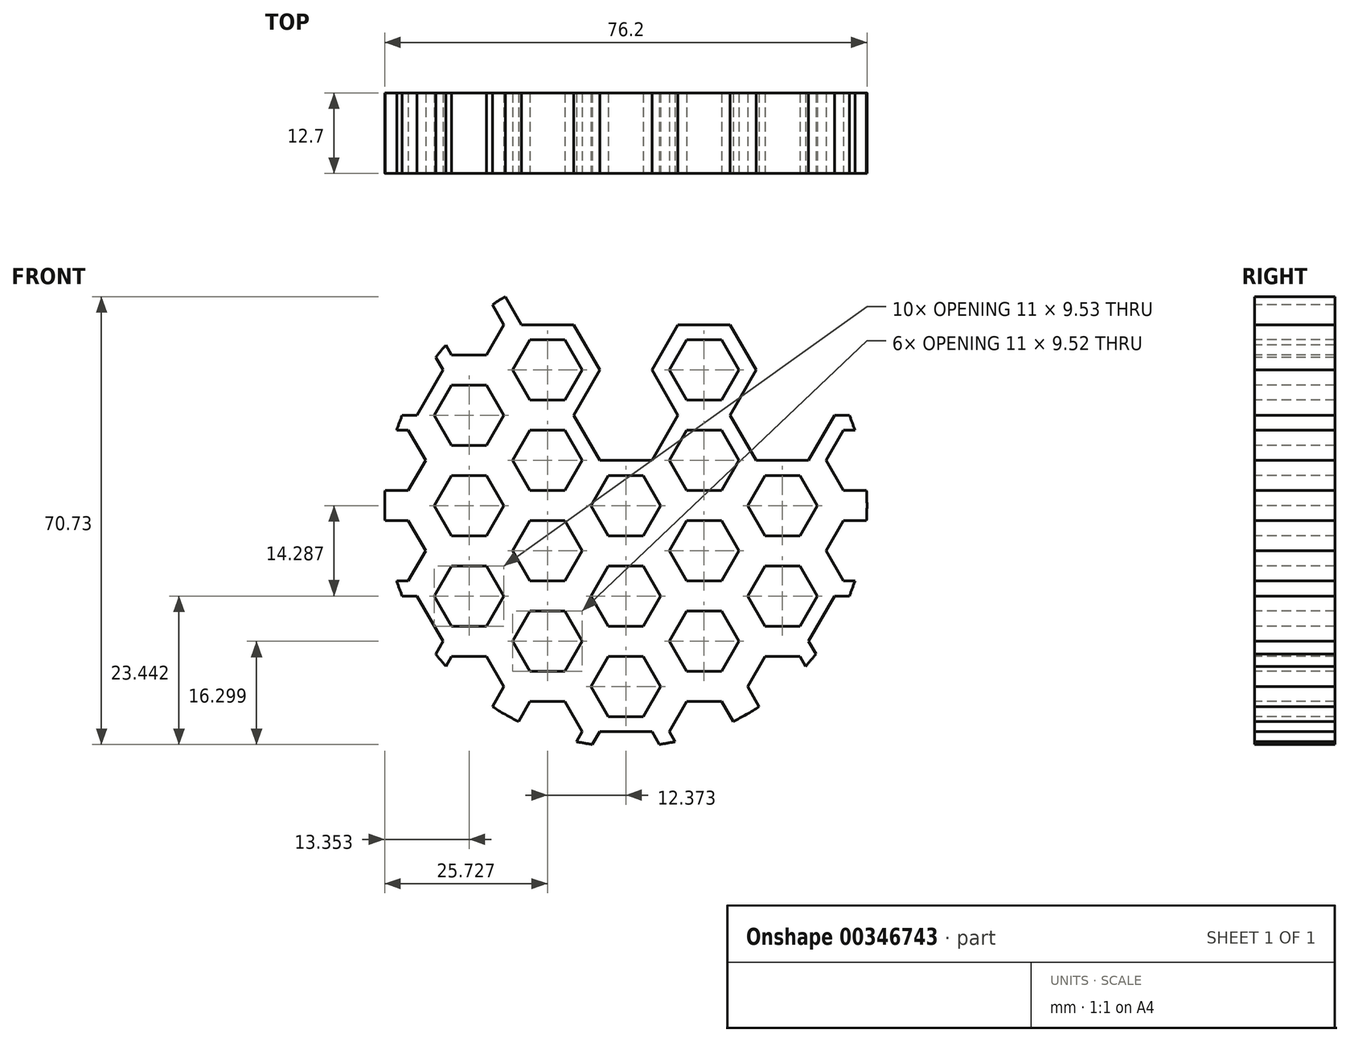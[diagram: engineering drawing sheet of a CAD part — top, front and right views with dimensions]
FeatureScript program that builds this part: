
annotation { "Feature Type Name" : "Feature", "Feature Type Description" : "" }
export const myFeature = defineFeature(function(context is Context, id is Id, definition is map)
    precondition{}
    {
        {
            var Q0;
            Q0=qCreatedBy(makeId("Front.planeOp"),FACE);
            var sketch = newSketch(context, id + "F0", { "sketchPlane" : qUnion([Q0])});
            skCircle(sketch, "E0.cCircle", {"center": v(0, 0) * mm, "radius": 4.76 * mm, "construction": true});
            skLineSegment(sketch, "E0.0", {"start": v(2.75, -4.76) * mm, "end": v(-2.75, -4.76) * mm});
            skLineSegment(sketch, "E0.1", {"start": v(-2.75, -4.76) * mm, "end": v(-5.5, 0) * mm});
            skLineSegment(sketch, "E0.2", {"start": v(-5.5, 0) * mm, "end": v(-2.75, 4.76) * mm});
            skLineSegment(sketch, "E0.3", {"start": v(-2.75, 4.76) * mm, "end": v(2.75, 4.76) * mm});
            skLineSegment(sketch, "E0.4", {"start": v(2.75, 4.76) * mm, "end": v(5.5, 0) * mm});
            skLineSegment(sketch, "E0.5", {"start": v(5.5, 0) * mm, "end": v(2.75, -4.76) * mm});
            skPoint(sketch, "E0.0.midPoint", {"position": v(0, -4.76) * mm});
            skCircle(sketch, "E1.cCircle", {"center": v(0, 0) * mm, "radius": 7.14 * mm, "construction": true});
            skLineSegment(sketch, "E1.0", {"start": v(4.12, -7.14) * mm, "end": v(-4.12, -7.14) * mm});
            skLineSegment(sketch, "E1.1", {"start": v(-4.12, -7.14) * mm, "end": v(-8.25, 0) * mm});
            skLineSegment(sketch, "E1.2", {"start": v(-8.25, 0) * mm, "end": v(-4.12, 7.14) * mm});
            skLineSegment(sketch, "E1.3", {"start": v(-4.12, 7.14) * mm, "end": v(4.12, 7.14) * mm});
            skLineSegment(sketch, "E1.4", {"start": v(4.12, 7.14) * mm, "end": v(8.25, 0) * mm});
            skLineSegment(sketch, "E1.5", {"start": v(8.25, 0) * mm, "end": v(4.12, -7.14) * mm});
            skPoint(sketch, "E1.0.midPoint", {"position": v(0, -7.14) * mm});
            skLineSegment(sketch, "E2.MirrorCS", {"start": v(17.87, 7.14) * mm, "end": v(15.12, 11.9) * mm});
            skLineSegment(sketch, "E3.MirrorCS", {"start": v(8.25, 0) * mm, "end": v(16.5, 0) * mm});
            skLineSegment(sketch, "E4.MirrorCS", {"start": v(15.12, 2.38) * mm, "end": v(17.87, 7.14) * mm});
            skPoint(sketch, "E5.MirrorP", {"position": v(16.5, 4.76) * mm});
            skLineSegment(sketch, "E6.MirrorCS", {"start": v(20.62, 7.14) * mm, "end": v(16.5, 14.29) * mm});
            skLineSegment(sketch, "E7.MirrorCS", {"start": v(16.5, 0) * mm, "end": v(20.62, 7.14) * mm});
            skLineSegment(sketch, "E8.MirrorCS", {"start": v(8.25, 14.29) * mm, "end": v(4.12, 7.14) * mm});
            skLineSegment(sketch, "E9.MirrorCS", {"start": v(16.5, 14.29) * mm, "end": v(8.25, 14.29) * mm});
            skLineSegment(sketch, "E10.MirrorCS", {"start": v(9.62, 11.9) * mm, "end": v(6.87, 7.14) * mm});
            skPoint(sketch, "E11.MirrorP", {"position": v(18.56, 3.57) * mm});
            skLineSegment(sketch, "E12.MirrorCS", {"start": v(6.87, 7.14) * mm, "end": v(9.62, 2.38) * mm});
            skLineSegment(sketch, "E13.MirrorCS", {"start": v(9.62, 2.38) * mm, "end": v(15.12, 2.38) * mm});
            skCircle(sketch, "E14.MirrorC", {"center": v(12.37, 7.14) * mm, "radius": 4.76 * mm, "construction": true});
            skCircle(sketch, "E15.MirrorC", {"center": v(12.37, 7.14) * mm, "radius": 7.14 * mm, "construction": true});
            skLineSegment(sketch, "E16.MirrorCS", {"start": v(15.12, 11.9) * mm, "end": v(9.62, 11.9) * mm});
            skLineSegment(sketch, "E17.MirrorCS", {"start": v(15.12, -2.38) * mm, "end": v(17.87, -7.14) * mm});
            skLineSegment(sketch, "E18.MirrorCS", {"start": v(20.62, -7.14) * mm, "end": v(16.5, -14.29) * mm});
            skPoint(sketch, "E19.MirrorP", {"position": v(16.5, -4.76) * mm});
            skLineSegment(sketch, "E20.MirrorCS", {"start": v(8.25, -14.29) * mm, "end": v(4.12, -7.14) * mm});
            skCircle(sketch, "E21.MirrorC", {"center": v(12.37, -7.14) * mm, "radius": 7.14 * mm, "construction": true});
            skLineSegment(sketch, "E22.MirrorCS", {"start": v(17.87, -7.14) * mm, "end": v(15.12, -11.9) * mm});
            skLineSegment(sketch, "E23.MirrorCS", {"start": v(4.12, -7.14) * mm, "end": v(8.25, 0) * mm});
            skLineSegment(sketch, "E24.MirrorCS", {"start": v(16.5, -14.29) * mm, "end": v(8.25, -14.29) * mm});
            skLineSegment(sketch, "E25.MirrorCS", {"start": v(6.87, -7.14) * mm, "end": v(9.62, -2.38) * mm});
            skLineSegment(sketch, "E26.MirrorCS", {"start": v(9.62, -11.9) * mm, "end": v(6.87, -7.14) * mm});
            skLineSegment(sketch, "E27.MirrorCS", {"start": v(16.5, 0) * mm, "end": v(20.62, -7.14) * mm});
            skCircle(sketch, "E28.MirrorC", {"center": v(12.37, -7.14) * mm, "radius": 4.76 * mm, "construction": true});
            skLineSegment(sketch, "E29.MirrorCS", {"start": v(15.12, -11.9) * mm, "end": v(9.62, -11.9) * mm});
            skLineSegment(sketch, "E30.MirrorCS", {"start": v(2.75, -4.76) * mm, "end": v(5.5, 0) * mm});
            skLineSegment(sketch, "E31.MirrorCS", {"start": v(9.62, -2.38) * mm, "end": v(15.12, -2.38) * mm});
            skPoint(sketch, "E32.MirrorP", {"position": v(18.56, -3.57) * mm});
            skCircle(sketch, "E33", {"center": v(0, 0) * mm, "radius": 38.1 * mm});
            skLineSegment(sketch, "E34.MirrorCS", {"start": v(15.12, 26.2) * mm, "end": v(17.87, 21.43) * mm});
            skLineSegment(sketch, "E35.MirrorCS", {"start": v(16.5, 28.58) * mm, "end": v(20.62, 21.43) * mm});
            skCircle(sketch, "E36.MirrorC", {"center": v(12.37, 21.43) * mm, "radius": 7.14 * mm, "construction": true});
            skLineSegment(sketch, "E37.MirrorCS", {"start": v(9.62, 16.67) * mm, "end": v(6.87, 21.43) * mm});
            skLineSegment(sketch, "E38.MirrorCS", {"start": v(9.62, 26.2) * mm, "end": v(15.12, 26.2) * mm});
            skLineSegment(sketch, "E39.MirrorCS", {"start": v(6.87, 21.43) * mm, "end": v(9.62, 26.2) * mm});
            skLineSegment(sketch, "E40.MirrorCS", {"start": v(4.12, 21.43) * mm, "end": v(8.25, 28.58) * mm});
            skCircle(sketch, "E41.MirrorC", {"center": v(12.37, 21.43) * mm, "radius": 4.76 * mm, "construction": true});
            skLineSegment(sketch, "E42.MirrorCS", {"start": v(20.62, 21.43) * mm, "end": v(16.5, 14.29) * mm});
            skPoint(sketch, "E43.MirrorP", {"position": v(16.5, 23.81) * mm});
            skPoint(sketch, "E44.MirrorP", {"position": v(18.56, 25) * mm});
            skLineSegment(sketch, "E45.MirrorCS", {"start": v(8.25, 14.29) * mm, "end": v(4.12, 21.43) * mm});
            skLineSegment(sketch, "E46.MirrorCS", {"start": v(15.12, 16.67) * mm, "end": v(9.62, 16.67) * mm});
            skLineSegment(sketch, "E47.MirrorCS", {"start": v(8.25, 28.58) * mm, "end": v(16.5, 28.58) * mm});
            skLineSegment(sketch, "E48.MirrorCS", {"start": v(17.87, 21.43) * mm, "end": v(15.12, 16.67) * mm});
            skLineSegment(sketch, "E49.MirrorCS", {"start": v(4.12, 7.14) * mm, "end": v(-4.12, 7.14) * mm});
            skLineSegment(sketch, "E50.MirrorCS", {"start": v(2.75, 19.05) * mm, "end": v(5.5, 14.29) * mm});
            skLineSegment(sketch, "E51.MirrorCS", {"start": v(4.12, 21.43) * mm, "end": v(8.25, 14.29) * mm});
            skCircle(sketch, "E52.MirrorC", {"center": v(0, 14.29) * mm, "radius": 7.14 * mm, "construction": true});
            skLineSegment(sketch, "E53.MirrorCS", {"start": v(-2.75, 9.52) * mm, "end": v(-5.5, 14.29) * mm});
            skLineSegment(sketch, "E54.MirrorCS", {"start": v(-2.75, 19.05) * mm, "end": v(2.75, 19.05) * mm});
            skLineSegment(sketch, "E55.MirrorCS", {"start": v(-5.5, 14.29) * mm, "end": v(-2.75, 19.05) * mm});
            skLineSegment(sketch, "E56.MirrorCS", {"start": v(-8.25, 14.29) * mm, "end": v(-4.12, 21.43) * mm});
            skCircle(sketch, "E57.MirrorC", {"center": v(0, 14.29) * mm, "radius": 4.76 * mm, "construction": true});
            skPoint(sketch, "E58.MirrorP", {"position": v(4.12, 16.67) * mm});
            skPoint(sketch, "E59.MirrorP", {"position": v(6.19, 17.86) * mm});
            skLineSegment(sketch, "E60.MirrorCS", {"start": v(-4.12, 7.14) * mm, "end": v(-8.25, 14.29) * mm});
            skLineSegment(sketch, "E61.MirrorCS", {"start": v(2.75, 9.53) * mm, "end": v(-2.75, 9.53) * mm});
            skLineSegment(sketch, "E62.MirrorCS", {"start": v(-4.12, 21.43) * mm, "end": v(4.12, 21.43) * mm});
            skLineSegment(sketch, "E63.MirrorCS", {"start": v(5.5, 14.29) * mm, "end": v(2.75, 9.53) * mm});
            skLineSegment(sketch, "E64.MirrorCS", {"start": v(4.12, 21.43) * mm, "end": v(-4.12, 21.43) * mm});
            skLineSegment(sketch, "E65.MirrorCS", {"start": v(2.75, 33.34) * mm, "end": v(5.5, 28.58) * mm});
            skLineSegment(sketch, "E66.MirrorCS", {"start": v(4.12, 35.72) * mm, "end": v(8.25, 28.58) * mm});
            skCircle(sketch, "E67.MirrorC", {"center": v(0, 28.58) * mm, "radius": 7.14 * mm, "construction": true});
            skLineSegment(sketch, "E68.MirrorCS", {"start": v(-2.75, 23.81) * mm, "end": v(-5.5, 28.57) * mm});
            skLineSegment(sketch, "E69.MirrorCS", {"start": v(-2.75, 33.34) * mm, "end": v(2.75, 33.34) * mm});
            skLineSegment(sketch, "E70.MirrorCS", {"start": v(-5.5, 28.57) * mm, "end": v(-2.75, 33.34) * mm});
            skLineSegment(sketch, "E71.MirrorCS", {"start": v(-8.25, 28.57) * mm, "end": v(-4.12, 35.72) * mm});
            skCircle(sketch, "E72.MirrorC", {"center": v(0, 28.58) * mm, "radius": 4.76 * mm, "construction": true});
            skLineSegment(sketch, "E73.MirrorCS", {"start": v(8.25, 28.58) * mm, "end": v(4.12, 21.43) * mm});
            skPoint(sketch, "E74.MirrorP", {"position": v(4.12, 30.96) * mm});
            skPoint(sketch, "E75.MirrorP", {"position": v(6.19, 32.15) * mm});
            skLineSegment(sketch, "E76.MirrorCS", {"start": v(-4.12, 21.43) * mm, "end": v(-8.25, 28.58) * mm});
            skLineSegment(sketch, "E77.MirrorCS", {"start": v(2.75, 23.81) * mm, "end": v(-2.75, 23.81) * mm});
            skLineSegment(sketch, "E78.MirrorCS", {"start": v(-4.12, 35.72) * mm, "end": v(4.12, 35.72) * mm});
            skLineSegment(sketch, "E79.MirrorCS", {"start": v(5.5, 28.58) * mm, "end": v(2.75, 23.81) * mm});
            skLineSegment(sketch, "E80.MirrorCS", {"start": v(28.87, -7.14) * mm, "end": v(20.62, -7.14) * mm});
            skLineSegment(sketch, "E81.MirrorCS", {"start": v(27.5, 4.76) * mm, "end": v(30.25, 0) * mm});
            skLineSegment(sketch, "E82.MirrorCS", {"start": v(28.87, 7.14) * mm, "end": v(33, 0) * mm});
            skCircle(sketch, "E83.MirrorC", {"center": v(24.75, 0) * mm, "radius": 7.14 * mm, "construction": true});
            skLineSegment(sketch, "E84.MirrorCS", {"start": v(22, -4.76) * mm, "end": v(19.25, 0) * mm});
            skLineSegment(sketch, "E85.MirrorCS", {"start": v(22, 4.76) * mm, "end": v(27.5, 4.76) * mm});
            skLineSegment(sketch, "E86.MirrorCS", {"start": v(19.25, 0) * mm, "end": v(22, 4.76) * mm});
            skCircle(sketch, "E87.MirrorC", {"center": v(24.75, 0) * mm, "radius": 4.76 * mm, "construction": true});
            skLineSegment(sketch, "E88.MirrorCS", {"start": v(33, 0) * mm, "end": v(28.87, -7.14) * mm});
            skPoint(sketch, "E89.MirrorP", {"position": v(28.87, 2.38) * mm});
            skPoint(sketch, "E90.MirrorP", {"position": v(30.93, 3.57) * mm});
            skLineSegment(sketch, "E91.MirrorCS", {"start": v(20.62, -7.14) * mm, "end": v(16.5, 0) * mm});
            skLineSegment(sketch, "E92.MirrorCS", {"start": v(27.5, -4.76) * mm, "end": v(22, -4.76) * mm});
            skLineSegment(sketch, "E93.MirrorCS", {"start": v(20.62, 7.14) * mm, "end": v(28.87, 7.14) * mm});
            skLineSegment(sketch, "E94.MirrorCS", {"start": v(30.25, 0) * mm, "end": v(27.5, -4.76) * mm});
            skLineSegment(sketch, "E95.MirrorCS", {"start": v(28.87, 7.14) * mm, "end": v(20.62, 7.14) * mm});
            skLineSegment(sketch, "E96.MirrorCS", {"start": v(27.5, 19.05) * mm, "end": v(30.25, 14.29) * mm});
            skLineSegment(sketch, "E97.MirrorCS", {"start": v(28.87, 21.43) * mm, "end": v(33, 14.29) * mm});
            skCircle(sketch, "E98.MirrorC", {"center": v(24.75, 14.29) * mm, "radius": 7.14 * mm, "construction": true});
            skLineSegment(sketch, "E99.MirrorCS", {"start": v(22, 9.53) * mm, "end": v(19.25, 14.29) * mm});
            skLineSegment(sketch, "E100.MirrorCS", {"start": v(22, 19.05) * mm, "end": v(27.5, 19.05) * mm});
            skLineSegment(sketch, "E101.MirrorCS", {"start": v(19.25, 14.29) * mm, "end": v(22, 19.05) * mm});
            skLineSegment(sketch, "E102.MirrorCS", {"start": v(16.5, 14.29) * mm, "end": v(20.62, 21.43) * mm});
            skCircle(sketch, "E103.MirrorC", {"center": v(24.75, 14.29) * mm, "radius": 4.76 * mm, "construction": true});
            skLineSegment(sketch, "E104.MirrorCS", {"start": v(33, 14.29) * mm, "end": v(28.87, 7.14) * mm});
            skPoint(sketch, "E105.MirrorP", {"position": v(28.87, 16.67) * mm});
            skPoint(sketch, "E106.MirrorP", {"position": v(30.93, 17.86) * mm});
            skLineSegment(sketch, "E107.MirrorCS", {"start": v(27.5, 9.53) * mm, "end": v(22, 9.53) * mm});
            skLineSegment(sketch, "E108.MirrorCS", {"start": v(20.62, 21.43) * mm, "end": v(28.87, 21.43) * mm});
            skLineSegment(sketch, "E109.MirrorCS", {"start": v(30.25, 14.29) * mm, "end": v(27.5, 9.53) * mm});
            skLineSegment(sketch, "E110.MirrorCS", {"start": v(28.87, 21.43) * mm, "end": v(20.62, 21.43) * mm});
            skArc(sketch, "E111.MirrorC", {"start": v(19.1, 32.96) * mm, "mid": v(20.07, 23.17) * mm, "end": v(29.9, 23.62) * mm, "construction": true});
            skLineSegment(sketch, "E112.MirrorCS", {"start": v(22, 23.81) * mm, "end": v(19.25, 28.57) * mm});
            skLineSegment(sketch, "E113.MirrorCS", {"start": v(19.25, 28.57) * mm, "end": v(21.07, 31.74) * mm});
            skLineSegment(sketch, "E114.MirrorCS", {"start": v(16.5, 28.57) * mm, "end": v(19.05, 33) * mm});
            skArc(sketch, "E115.MirrorC", {"start": v(21.15, 31.7) * mm, "mid": v(21.63, 24.97) * mm, "end": v(28.35, 25.46) * mm, "construction": true});
            skLineSegment(sketch, "E116.MirrorCS", {"start": v(20.62, 21.43) * mm, "end": v(16.5, 28.57) * mm});
            skLineSegment(sketch, "E117.MirrorCS", {"start": v(27.5, 23.81) * mm, "end": v(22, 23.81) * mm});
            skLineSegment(sketch, "E118.MirrorCS", {"start": v(16.5, 28.58) * mm, "end": v(8.25, 28.58) * mm});
            skArc(sketch, "E119.MirrorC", {"start": v(5.5, 37.7) * mm, "mid": v(10.03, 28.97) * mm, "end": v(19, 33.03) * mm, "construction": true});
            skLineSegment(sketch, "E120.MirrorCS", {"start": v(9.62, 30.96) * mm, "end": v(6.87, 35.72) * mm});
            skLineSegment(sketch, "E121.MirrorCS", {"start": v(6.87, 35.72) * mm, "end": v(7.78, 37.3) * mm});
            skLineSegment(sketch, "E122.MirrorCS", {"start": v(4.12, 35.72) * mm, "end": v(5.29, 37.73) * mm});
            skArc(sketch, "E123.MirrorC", {"start": v(7.87, 37.28) * mm, "mid": v(10.81, 31.22) * mm, "end": v(16.87, 34.16) * mm, "construction": true});
            skLineSegment(sketch, "E124.MirrorCS", {"start": v(19.05, 33) * mm, "end": v(16.5, 28.57) * mm});
            skLineSegment(sketch, "E125.MirrorCS", {"start": v(8.25, 28.57) * mm, "end": v(4.12, 35.72) * mm});
            skLineSegment(sketch, "E126.MirrorCS", {"start": v(15.12, 30.96) * mm, "end": v(9.62, 30.96) * mm});
            skLineSegment(sketch, "E127.MirrorCS", {"start": v(16.95, 34.12) * mm, "end": v(15.12, 30.96) * mm});
            skLineSegment(sketch, "E128.MirrorCS", {"start": v(38.1, 0) * mm, "end": v(33, 0) * mm});
            skArc(sketch, "E129.MirrorC", {"start": v(35.4, 14.08) * mm, "mid": v(30.1, 5.8) * mm, "end": v(38.1, 0.07) * mm, "construction": true});
            skLineSegment(sketch, "E130.MirrorCS", {"start": v(34.37, 2.38) * mm, "end": v(31.62, 7.14) * mm});
            skLineSegment(sketch, "E131.MirrorCS", {"start": v(34.37, 11.9) * mm, "end": v(36.2, 11.9) * mm});
            skLineSegment(sketch, "E132.MirrorCS", {"start": v(31.62, 7.14) * mm, "end": v(34.37, 11.9) * mm});
            skLineSegment(sketch, "E133.MirrorCS", {"start": v(28.87, 7.14) * mm, "end": v(33, 14.29) * mm});
            skArc(sketch, "E134.MirrorC", {"start": v(33, 9.53) * mm, "mid": v(33.24, 4.38) * mm, "end": v(38.02, 2.47) * mm, "construction": true});
            skLineSegment(sketch, "E135.MirrorCS", {"start": v(33, 0) * mm, "end": v(28.87, 7.14) * mm});
            skLineSegment(sketch, "E136.MirrorCS", {"start": v(38.03, 2.38) * mm, "end": v(34.37, 2.38) * mm});
            skLineSegment(sketch, "E137.MirrorCS", {"start": v(33, 14.29) * mm, "end": v(35.32, 14.29) * mm});
            skArc(sketch, "E138.MirrorC", {"start": v(30.2, 23.22) * mm, "mid": v(30.93, 17.86) * mm, "end": v(35.21, 14.55) * mm, "construction": true});
            skLineSegment(sketch, "E139.MirrorCS", {"start": v(33, 14.29) * mm, "end": v(28.87, 21.43) * mm});
            skLineSegment(sketch, "E140.MirrorCS", {"start": v(-8.25, 14.29) * mm, "end": v(-16.5, 14.29) * mm});
            skLineSegment(sketch, "E141.MirrorCS", {"start": v(-9.62, 26.2) * mm, "end": v(-6.87, 21.43) * mm});
            skLineSegment(sketch, "E142.MirrorCS", {"start": v(-8.25, 28.58) * mm, "end": v(-4.12, 21.43) * mm});
            skCircle(sketch, "E143.MirrorC", {"center": v(-12.37, 21.43) * mm, "radius": 7.14 * mm, "construction": true});
            skLineSegment(sketch, "E144.MirrorCS", {"start": v(-15.12, 16.67) * mm, "end": v(-17.87, 21.43) * mm});
            skLineSegment(sketch, "E145.MirrorCS", {"start": v(-15.12, 26.2) * mm, "end": v(-9.62, 26.2) * mm});
            skLineSegment(sketch, "E146.MirrorCS", {"start": v(-17.87, 21.43) * mm, "end": v(-15.12, 26.2) * mm});
            skLineSegment(sketch, "E147.MirrorCS", {"start": v(-20.62, 21.43) * mm, "end": v(-16.5, 28.58) * mm});
            skCircle(sketch, "E148.MirrorC", {"center": v(-12.37, 21.43) * mm, "radius": 4.76 * mm, "construction": true});
            skLineSegment(sketch, "E149.MirrorCS", {"start": v(-4.12, 21.43) * mm, "end": v(-8.25, 14.29) * mm});
            skPoint(sketch, "E150.MirrorP", {"position": v(-8.25, 23.81) * mm});
            skPoint(sketch, "E151.MirrorP", {"position": v(-6.19, 25) * mm});
            skLineSegment(sketch, "E152.MirrorCS", {"start": v(-16.5, 14.29) * mm, "end": v(-20.62, 21.43) * mm});
            skLineSegment(sketch, "E153.MirrorCS", {"start": v(-9.62, 16.67) * mm, "end": v(-15.12, 16.67) * mm});
            skLineSegment(sketch, "E154.MirrorCS", {"start": v(-16.5, 28.58) * mm, "end": v(-8.25, 28.58) * mm});
            skLineSegment(sketch, "E155.MirrorCS", {"start": v(-6.87, 21.43) * mm, "end": v(-9.62, 16.67) * mm});
            skLineSegment(sketch, "E156.MirrorCS", {"start": v(-8.25, 28.57) * mm, "end": v(-16.5, 28.57) * mm});
            skArc(sketch, "E157.MirrorC", {"start": v(-19, 33.03) * mm, "mid": v(-10.03, 28.97) * mm, "end": v(-5.5, 37.7) * mm, "construction": true});
            skLineSegment(sketch, "E158.MirrorCS", {"start": v(-15.12, 30.96) * mm, "end": v(-16.95, 34.12) * mm});
            skArc(sketch, "E159.MirrorC", {"start": v(-16.87, 34.16) * mm, "mid": v(-10.81, 31.22) * mm, "end": v(-7.87, 37.28) * mm, "construction": true});
            skLineSegment(sketch, "E160.MirrorCS", {"start": v(-4.12, 35.72) * mm, "end": v(-8.25, 28.57) * mm});
            skLineSegment(sketch, "E161.MirrorCS", {"start": v(-16.5, 28.57) * mm, "end": v(-19.05, 33) * mm});
            skLineSegment(sketch, "E162.MirrorCS", {"start": v(-9.62, 30.96) * mm, "end": v(-15.12, 30.96) * mm});
            skLineSegment(sketch, "E163.MirrorCS", {"start": v(-6.87, 35.72) * mm, "end": v(-9.62, 30.96) * mm});
            skLineSegment(sketch, "E164.MirrorCS", {"start": v(4.12, 35.72) * mm, "end": v(-4.12, 35.72) * mm});
            skArc(sketch, "E165.MirrorC", {"start": v(-5, 37.77) * mm, "mid": v(-2.7, 36.25) * mm, "end": v(0, 35.72) * mm, "construction": true});
            skLineSegment(sketch, "E166.MirrorCS", {"start": v(-4.12, 35.72) * mm, "end": v(-5.29, 37.73) * mm});
            skLineSegment(sketch, "E167.MirrorCS", {"start": v(-20.62, 21.43) * mm, "end": v(-28.87, 21.43) * mm});
            skLineSegment(sketch, "E168.MirrorCS", {"start": v(-21.07, 31.74) * mm, "end": v(-19.25, 28.58) * mm});
            skLineSegment(sketch, "E169.MirrorCS", {"start": v(-19.05, 33) * mm, "end": v(-16.5, 28.58) * mm});
            skLineSegment(sketch, "E170.MirrorCS", {"start": v(-27.5, 23.81) * mm, "end": v(-28.4, 25.39) * mm});
            skLineSegment(sketch, "E171.MirrorCS", {"start": v(-16.5, 28.58) * mm, "end": v(-20.62, 21.43) * mm});
            skPoint(sketch, "E172.MirrorP", {"position": v(-20.62, 30.96) * mm});
            skPoint(sketch, "E173.MirrorP", {"position": v(-18.56, 32.15) * mm});
            skLineSegment(sketch, "E174.MirrorCS", {"start": v(-28.87, 21.43) * mm, "end": v(-30.03, 23.44) * mm});
            skLineSegment(sketch, "E175.MirrorCS", {"start": v(-22, 23.81) * mm, "end": v(-27.5, 23.81) * mm});
            skLineSegment(sketch, "E176.MirrorCS", {"start": v(-19.25, 28.58) * mm, "end": v(-22, 23.81) * mm});
            skLineSegment(sketch, "E177.MirrorCS", {"start": v(-20.62, 7.14) * mm, "end": v(-28.87, 7.14) * mm});
            skLineSegment(sketch, "E178.MirrorCS", {"start": v(-22, 19.05) * mm, "end": v(-19.25, 14.29) * mm});
            skLineSegment(sketch, "E179.MirrorCS", {"start": v(-20.62, 21.43) * mm, "end": v(-16.5, 14.29) * mm});
            skCircle(sketch, "E180.MirrorC", {"center": v(-24.75, 14.29) * mm, "radius": 7.14 * mm, "construction": true});
            skLineSegment(sketch, "E181.MirrorCS", {"start": v(-27.5, 9.52) * mm, "end": v(-30.25, 14.29) * mm});
            skLineSegment(sketch, "E182.MirrorCS", {"start": v(-27.5, 19.05) * mm, "end": v(-22, 19.05) * mm});
            skLineSegment(sketch, "E183.MirrorCS", {"start": v(-30.25, 14.29) * mm, "end": v(-27.5, 19.05) * mm});
            skLineSegment(sketch, "E184.MirrorCS", {"start": v(-33, 14.29) * mm, "end": v(-28.87, 21.43) * mm});
            skCircle(sketch, "E185.MirrorC", {"center": v(-24.75, 14.29) * mm, "radius": 4.76 * mm, "construction": true});
            skLineSegment(sketch, "E186.MirrorCS", {"start": v(-16.5, 14.29) * mm, "end": v(-20.62, 7.14) * mm});
            skPoint(sketch, "E187.MirrorP", {"position": v(-20.62, 16.67) * mm});
            skPoint(sketch, "E188.MirrorP", {"position": v(-18.56, 17.86) * mm});
            skLineSegment(sketch, "E189.MirrorCS", {"start": v(-28.87, 7.14) * mm, "end": v(-33, 14.29) * mm});
            skLineSegment(sketch, "E190.MirrorCS", {"start": v(-22, 9.53) * mm, "end": v(-27.5, 9.53) * mm});
            skLineSegment(sketch, "E191.MirrorCS", {"start": v(-28.87, 21.43) * mm, "end": v(-20.62, 21.43) * mm});
            skLineSegment(sketch, "E192.MirrorCS", {"start": v(-19.25, 14.29) * mm, "end": v(-22, 9.53) * mm});
            skLineSegment(sketch, "E193.MirrorCS", {"start": v(-8.25, 0) * mm, "end": v(-16.5, 0) * mm});
            skLineSegment(sketch, "E194.MirrorCS", {"start": v(-9.62, 11.9) * mm, "end": v(-6.87, 7.14) * mm});
            skLineSegment(sketch, "E195.MirrorCS", {"start": v(-8.25, 14.29) * mm, "end": v(-4.12, 7.14) * mm});
            skCircle(sketch, "E196.MirrorC", {"center": v(-12.37, 7.14) * mm, "radius": 7.14 * mm, "construction": true});
            skLineSegment(sketch, "E197.MirrorCS", {"start": v(-15.12, 2.38) * mm, "end": v(-17.87, 7.14) * mm});
            skLineSegment(sketch, "E198.MirrorCS", {"start": v(-15.12, 11.9) * mm, "end": v(-9.62, 11.9) * mm});
            skLineSegment(sketch, "E199.MirrorCS", {"start": v(-17.87, 7.14) * mm, "end": v(-15.12, 11.9) * mm});
            skLineSegment(sketch, "E200.MirrorCS", {"start": v(-20.62, 7.14) * mm, "end": v(-16.5, 14.29) * mm});
            skCircle(sketch, "E201.MirrorC", {"center": v(-12.37, 7.14) * mm, "radius": 4.76 * mm, "construction": true});
            skLineSegment(sketch, "E202.MirrorCS", {"start": v(-4.12, 7.14) * mm, "end": v(-8.25, 0) * mm});
            skPoint(sketch, "E203.MirrorP", {"position": v(-8.25, 9.52) * mm});
            skPoint(sketch, "E204.MirrorP", {"position": v(-6.19, 10.72) * mm});
            skLineSegment(sketch, "E205.MirrorCS", {"start": v(-16.5, 0) * mm, "end": v(-20.62, 7.14) * mm});
            skLineSegment(sketch, "E206.MirrorCS", {"start": v(-9.62, 2.38) * mm, "end": v(-15.12, 2.38) * mm});
            skLineSegment(sketch, "E207.MirrorCS", {"start": v(-16.5, 14.29) * mm, "end": v(-8.25, 14.29) * mm});
            skLineSegment(sketch, "E208.MirrorCS", {"start": v(-6.87, 7.14) * mm, "end": v(-9.62, 2.38) * mm});
            skLineSegment(sketch, "E209.MirrorCS", {"start": v(-33, 14.29) * mm, "end": v(-35.32, 14.29) * mm});
            skArc(sketch, "E210.MirrorC", {"start": v(-35.21, 14.55) * mm, "mid": v(-30.93, 17.86) * mm, "end": v(-30.2, 23.22) * mm, "construction": true});
            skLineSegment(sketch, "E211.MirrorCS", {"start": v(-28.87, 21.43) * mm, "end": v(-33, 14.29) * mm});
            skLineSegment(sketch, "E212.MirrorCS", {"start": v(-33, 0) * mm, "end": v(-38.1, 0) * mm});
            skLineSegment(sketch, "E213.MirrorCS", {"start": v(-34.37, 11.9) * mm, "end": v(-31.62, 7.14) * mm});
            skLineSegment(sketch, "E214.MirrorCS", {"start": v(-33, 14.29) * mm, "end": v(-28.87, 7.14) * mm});
            skArc(sketch, "E215.MirrorC", {"start": v(-38.1, 0.07) * mm, "mid": v(-30.1, 5.8) * mm, "end": v(-35.4, 14.08) * mm, "construction": true});
            skArc(sketch, "E216.MirrorC", {"start": v(-38.02, 2.47) * mm, "mid": v(-32.44, 6.24) * mm, "end": v(-36.22, 11.82) * mm, "construction": true});
            skLineSegment(sketch, "E217.MirrorCS", {"start": v(-28.87, 7.14) * mm, "end": v(-33, 0) * mm});
            skPoint(sketch, "E218.MirrorP", {"position": v(-33, 9.52) * mm});
            skPoint(sketch, "E219.MirrorP", {"position": v(-30.93, 10.72) * mm});
            skLineSegment(sketch, "E220.MirrorCS", {"start": v(-34.37, 2.38) * mm, "end": v(-38.03, 2.38) * mm});
            skLineSegment(sketch, "E221.MirrorCS", {"start": v(-31.62, 7.14) * mm, "end": v(-34.37, 2.38) * mm});
            skLineSegment(sketch, "E222.MirrorCS", {"start": v(-20.62, -7.14) * mm, "end": v(-28.87, -7.14) * mm});
            skLineSegment(sketch, "E223.MirrorCS", {"start": v(-22, 4.76) * mm, "end": v(-19.25, 0) * mm});
            skLineSegment(sketch, "E224.MirrorCS", {"start": v(-20.62, 7.14) * mm, "end": v(-16.5, 0) * mm});
            skCircle(sketch, "E225.MirrorC", {"center": v(-24.75, 0) * mm, "radius": 7.14 * mm, "construction": true});
            skLineSegment(sketch, "E226.MirrorCS", {"start": v(-27.5, -4.76) * mm, "end": v(-30.25, 0) * mm});
            skLineSegment(sketch, "E227.MirrorCS", {"start": v(-27.5, 4.76) * mm, "end": v(-22, 4.76) * mm});
            skLineSegment(sketch, "E228.MirrorCS", {"start": v(-30.25, 0) * mm, "end": v(-27.5, 4.76) * mm});
            skLineSegment(sketch, "E229.MirrorCS", {"start": v(-33, 0) * mm, "end": v(-28.87, 7.14) * mm});
            skCircle(sketch, "E230.MirrorC", {"center": v(-24.75, 0) * mm, "radius": 4.76 * mm, "construction": true});
            skLineSegment(sketch, "E231.MirrorCS", {"start": v(-16.5, 0) * mm, "end": v(-20.62, -7.14) * mm});
            skPoint(sketch, "E232.MirrorP", {"position": v(-20.62, 2.38) * mm});
            skPoint(sketch, "E233.MirrorP", {"position": v(-18.56, 3.57) * mm});
            skLineSegment(sketch, "E234.MirrorCS", {"start": v(-28.87, -7.14) * mm, "end": v(-33, 0) * mm});
            skLineSegment(sketch, "E235.MirrorCS", {"start": v(-22, -4.76) * mm, "end": v(-27.5, -4.76) * mm});
            skLineSegment(sketch, "E236.MirrorCS", {"start": v(-28.87, 7.14) * mm, "end": v(-20.62, 7.14) * mm});
            skLineSegment(sketch, "E237.MirrorCS", {"start": v(-19.25, 0) * mm, "end": v(-22, -4.76) * mm});
            skLineSegment(sketch, "E238.MirrorCS", {"start": v(-33, -14.29) * mm, "end": v(-35.32, -14.29) * mm});
            skLineSegment(sketch, "E239.MirrorCS", {"start": v(-34.37, -2.38) * mm, "end": v(-31.62, -7.14) * mm});
            skLineSegment(sketch, "E240.MirrorCS", {"start": v(-33, 0) * mm, "end": v(-28.87, -7.14) * mm});
            skArc(sketch, "E241.MirrorC", {"start": v(-35.4, -14.08) * mm, "mid": v(-30.1, -5.8) * mm, "end": v(-38.1, -0.07) * mm, "construction": true});
            skLineSegment(sketch, "E242.MirrorCS", {"start": v(-38.03, -2.38) * mm, "end": v(-34.37, -2.38) * mm});
            skArc(sketch, "E243.MirrorC", {"start": v(-36.22, -11.82) * mm, "mid": v(-32.44, -6.24) * mm, "end": v(-38.02, -2.47) * mm, "construction": true});
            skLineSegment(sketch, "E244.MirrorCS", {"start": v(-28.87, -7.14) * mm, "end": v(-33, -14.29) * mm});
            skPoint(sketch, "E245.MirrorP", {"position": v(-33, -4.76) * mm});
            skPoint(sketch, "E246.MirrorP", {"position": v(-30.93, -3.57) * mm});
            skLineSegment(sketch, "E247.MirrorCS", {"start": v(-34.37, -11.9) * mm, "end": v(-36.2, -11.9) * mm});
            skLineSegment(sketch, "E248.MirrorCS", {"start": v(-38.1, 0) * mm, "end": v(-33, 0) * mm});
            skLineSegment(sketch, "E249.MirrorCS", {"start": v(-31.62, -7.14) * mm, "end": v(-34.37, -11.9) * mm});
            skLineSegment(sketch, "E250.MirrorCS", {"start": v(-8.25, -14.29) * mm, "end": v(-16.5, -14.29) * mm});
            skLineSegment(sketch, "E251.MirrorCS", {"start": v(-9.62, -2.38) * mm, "end": v(-6.87, -7.14) * mm});
            skLineSegment(sketch, "E252.MirrorCS", {"start": v(-8.25, 0) * mm, "end": v(-4.12, -7.14) * mm});
            skCircle(sketch, "E253.MirrorC", {"center": v(-12.37, -7.14) * mm, "radius": 7.14 * mm, "construction": true});
            skLineSegment(sketch, "E254.MirrorCS", {"start": v(-15.12, -11.9) * mm, "end": v(-17.87, -7.14) * mm});
            skLineSegment(sketch, "E255.MirrorCS", {"start": v(-15.12, -2.38) * mm, "end": v(-9.62, -2.38) * mm});
            skLineSegment(sketch, "E256.MirrorCS", {"start": v(-17.87, -7.14) * mm, "end": v(-15.12, -2.38) * mm});
            skLineSegment(sketch, "E257.MirrorCS", {"start": v(-20.62, -7.14) * mm, "end": v(-16.5, 0) * mm});
            skCircle(sketch, "E258.MirrorC", {"center": v(-12.37, -7.14) * mm, "radius": 4.76 * mm, "construction": true});
            skLineSegment(sketch, "E259.MirrorCS", {"start": v(-4.12, -7.14) * mm, "end": v(-8.25, -14.29) * mm});
            skPoint(sketch, "E260.MirrorP", {"position": v(-8.25, -4.76) * mm});
            skPoint(sketch, "E261.MirrorP", {"position": v(-6.19, -3.57) * mm});
            skLineSegment(sketch, "E262.MirrorCS", {"start": v(-16.5, -14.29) * mm, "end": v(-20.62, -7.14) * mm});
            skLineSegment(sketch, "E263.MirrorCS", {"start": v(-9.62, -11.9) * mm, "end": v(-15.12, -11.9) * mm});
            skLineSegment(sketch, "E264.MirrorCS", {"start": v(-16.5, 0) * mm, "end": v(-8.25, 0) * mm});
            skLineSegment(sketch, "E265.MirrorCS", {"start": v(-6.87, -7.14) * mm, "end": v(-9.62, -11.9) * mm});
            skArc(sketch, "E266.MirrorC", {"start": v(38.1, -0.07) * mm, "mid": v(30.1, -5.8) * mm, "end": v(35.4, -14.08) * mm, "construction": true});
            skLineSegment(sketch, "E267.MirrorCS", {"start": v(34.37, -11.9) * mm, "end": v(31.62, -7.14) * mm});
            skLineSegment(sketch, "E268.MirrorCS", {"start": v(34.37, -2.38) * mm, "end": v(38.03, -2.38) * mm});
            skLineSegment(sketch, "E269.MirrorCS", {"start": v(31.62, -7.14) * mm, "end": v(34.37, -2.38) * mm});
            skLineSegment(sketch, "E270.MirrorCS", {"start": v(28.87, -7.14) * mm, "end": v(33, 0) * mm});
            skArc(sketch, "E271.MirrorC", {"start": v(38.02, -2.47) * mm, "mid": v(32.44, -6.24) * mm, "end": v(36.22, -11.82) * mm, "construction": true});
            skLineSegment(sketch, "E272.MirrorCS", {"start": v(33, -14.29) * mm, "end": v(28.87, -7.14) * mm});
            skLineSegment(sketch, "E273.MirrorCS", {"start": v(33, 0) * mm, "end": v(38.1, 0) * mm});
            skLineSegment(sketch, "E274.MirrorCS", {"start": v(28.87, -21.43) * mm, "end": v(20.62, -21.43) * mm});
            skLineSegment(sketch, "E275.MirrorCS", {"start": v(27.5, -9.53) * mm, "end": v(30.25, -14.29) * mm});
            skLineSegment(sketch, "E276.MirrorCS", {"start": v(28.87, -7.14) * mm, "end": v(33, -14.29) * mm});
            skCircle(sketch, "E277.MirrorC", {"center": v(24.75, -14.29) * mm, "radius": 7.14 * mm, "construction": true});
            skLineSegment(sketch, "E278.MirrorCS", {"start": v(22, -19.05) * mm, "end": v(19.25, -14.29) * mm});
            skLineSegment(sketch, "E279.MirrorCS", {"start": v(22, -9.53) * mm, "end": v(27.5, -9.52) * mm});
            skLineSegment(sketch, "E280.MirrorCS", {"start": v(19.25, -14.29) * mm, "end": v(22, -9.52) * mm});
            skLineSegment(sketch, "E281.MirrorCS", {"start": v(16.5, -14.29) * mm, "end": v(20.62, -7.14) * mm});
            skCircle(sketch, "E282.MirrorC", {"center": v(24.75, -14.29) * mm, "radius": 4.76 * mm, "construction": true});
            skLineSegment(sketch, "E283.MirrorCS", {"start": v(33, -14.29) * mm, "end": v(28.87, -21.43) * mm});
            skPoint(sketch, "E284.MirrorP", {"position": v(28.87, -11.9) * mm});
            skPoint(sketch, "E285.MirrorP", {"position": v(30.93, -10.72) * mm});
            skLineSegment(sketch, "E286.MirrorCS", {"start": v(20.62, -21.43) * mm, "end": v(16.5, -14.29) * mm});
            skLineSegment(sketch, "E287.MirrorCS", {"start": v(27.5, -19.05) * mm, "end": v(22, -19.05) * mm});
            skLineSegment(sketch, "E288.MirrorCS", {"start": v(20.62, -7.14) * mm, "end": v(28.87, -7.14) * mm});
            skLineSegment(sketch, "E289.MirrorCS", {"start": v(30.25, -14.29) * mm, "end": v(27.5, -19.05) * mm});
            skLineSegment(sketch, "E290.MirrorCS", {"start": v(4.12, -21.43) * mm, "end": v(-4.12, -21.43) * mm});
            skLineSegment(sketch, "E291.MirrorCS", {"start": v(2.75, -9.53) * mm, "end": v(5.5, -14.29) * mm});
            skLineSegment(sketch, "E292.MirrorCS", {"start": v(4.12, -7.14) * mm, "end": v(8.25, -14.29) * mm});
            skCircle(sketch, "E293.MirrorC", {"center": v(0, -14.29) * mm, "radius": 7.14 * mm, "construction": true});
            skLineSegment(sketch, "E294.MirrorCS", {"start": v(-2.75, -19.05) * mm, "end": v(-5.5, -14.29) * mm});
            skLineSegment(sketch, "E295.MirrorCS", {"start": v(-2.75, -9.53) * mm, "end": v(2.75, -9.53) * mm});
            skLineSegment(sketch, "E296.MirrorCS", {"start": v(-5.5, -14.29) * mm, "end": v(-2.75, -9.53) * mm});
            skLineSegment(sketch, "E297.MirrorCS", {"start": v(-8.25, -14.29) * mm, "end": v(-4.12, -7.14) * mm});
            skCircle(sketch, "E298.MirrorC", {"center": v(0, -14.29) * mm, "radius": 4.76 * mm, "construction": true});
            skLineSegment(sketch, "E299.MirrorCS", {"start": v(8.25, -14.29) * mm, "end": v(4.12, -21.43) * mm});
            skPoint(sketch, "E300.MirrorP", {"position": v(4.12, -11.9) * mm});
            skPoint(sketch, "E301.MirrorP", {"position": v(6.19, -10.72) * mm});
            skLineSegment(sketch, "E302.MirrorCS", {"start": v(-4.12, -21.43) * mm, "end": v(-8.25, -14.29) * mm});
            skLineSegment(sketch, "E303.MirrorCS", {"start": v(2.75, -19.05) * mm, "end": v(-2.75, -19.05) * mm});
            skLineSegment(sketch, "E304.MirrorCS", {"start": v(-4.12, -7.14) * mm, "end": v(4.12, -7.14) * mm});
            skLineSegment(sketch, "E305.MirrorCS", {"start": v(5.5, -14.29) * mm, "end": v(2.75, -19.05) * mm});
            skArc(sketch, "E306.MirrorC", {"start": v(35.21, -14.55) * mm, "mid": v(30.93, -17.86) * mm, "end": v(30.2, -23.22) * mm, "construction": true});
            skLineSegment(sketch, "E307.MirrorCS", {"start": v(28.87, -21.43) * mm, "end": v(33, -14.29) * mm});
            skLineSegment(sketch, "E308.MirrorCS", {"start": v(33, -14.29) * mm, "end": v(35.32, -14.29) * mm});
            skLineSegment(sketch, "E309.MirrorCS", {"start": v(27.5, -23.81) * mm, "end": v(28.4, -25.39) * mm});
            skLineSegment(sketch, "E310.MirrorCS", {"start": v(28.87, -21.43) * mm, "end": v(30.03, -23.44) * mm});
            skArc(sketch, "E311.MirrorC", {"start": v(29.9, -23.62) * mm, "mid": v(20.07, -23.17) * mm, "end": v(19.1, -32.96) * mm, "construction": true});
            skLineSegment(sketch, "E312.MirrorCS", {"start": v(21.07, -31.74) * mm, "end": v(19.25, -28.58) * mm});
            skLineSegment(sketch, "E313.MirrorCS", {"start": v(22, -23.81) * mm, "end": v(27.5, -23.81) * mm});
            skLineSegment(sketch, "E314.MirrorCS", {"start": v(19.25, -28.58) * mm, "end": v(22, -23.81) * mm});
            skLineSegment(sketch, "E315.MirrorCS", {"start": v(16.5, -28.58) * mm, "end": v(20.62, -21.43) * mm});
            skArc(sketch, "E316.MirrorC", {"start": v(28.35, -25.46) * mm, "mid": v(21.63, -24.97) * mm, "end": v(21.15, -31.7) * mm, "construction": true});
            skLineSegment(sketch, "E317.MirrorCS", {"start": v(19.05, -33) * mm, "end": v(16.5, -28.58) * mm});
            skLineSegment(sketch, "E318.MirrorCS", {"start": v(20.62, -21.43) * mm, "end": v(28.87, -21.43) * mm});
            skLineSegment(sketch, "E319.MirrorCS", {"start": v(16.5, -28.58) * mm, "end": v(8.25, -28.58) * mm});
            skLineSegment(sketch, "E320.MirrorCS", {"start": v(15.12, -16.67) * mm, "end": v(17.87, -21.43) * mm});
            skLineSegment(sketch, "E321.MirrorCS", {"start": v(16.5, -14.29) * mm, "end": v(20.62, -21.43) * mm});
            skCircle(sketch, "E322.MirrorC", {"center": v(12.37, -21.43) * mm, "radius": 7.14 * mm, "construction": true});
            skLineSegment(sketch, "E323.MirrorCS", {"start": v(9.62, -26.2) * mm, "end": v(6.87, -21.43) * mm});
            skLineSegment(sketch, "E324.MirrorCS", {"start": v(9.62, -16.67) * mm, "end": v(15.12, -16.67) * mm});
            skLineSegment(sketch, "E325.MirrorCS", {"start": v(6.87, -21.43) * mm, "end": v(9.62, -16.67) * mm});
            skLineSegment(sketch, "E326.MirrorCS", {"start": v(4.12, -21.43) * mm, "end": v(8.25, -14.29) * mm});
            skCircle(sketch, "E327.MirrorC", {"center": v(12.37, -21.43) * mm, "radius": 4.76 * mm, "construction": true});
            skLineSegment(sketch, "E328.MirrorCS", {"start": v(20.62, -21.43) * mm, "end": v(16.5, -28.58) * mm});
            skPoint(sketch, "E329.MirrorP", {"position": v(16.5, -19.05) * mm});
            skPoint(sketch, "E330.MirrorP", {"position": v(18.56, -17.86) * mm});
            skLineSegment(sketch, "E331.MirrorCS", {"start": v(8.25, -28.58) * mm, "end": v(4.12, -21.43) * mm});
            skLineSegment(sketch, "E332.MirrorCS", {"start": v(15.12, -26.2) * mm, "end": v(9.62, -26.2) * mm});
            skLineSegment(sketch, "E333.MirrorCS", {"start": v(8.25, -14.29) * mm, "end": v(16.5, -14.29) * mm});
            skLineSegment(sketch, "E334.MirrorCS", {"start": v(17.87, -21.43) * mm, "end": v(15.12, -26.2) * mm});
            skLineSegment(sketch, "E335.MirrorCS", {"start": v(-20.62, -21.43) * mm, "end": v(-28.87, -21.43) * mm});
            skLineSegment(sketch, "E336.MirrorCS", {"start": v(-22, -9.53) * mm, "end": v(-19.25, -14.29) * mm});
            skLineSegment(sketch, "E337.MirrorCS", {"start": v(-20.62, -7.14) * mm, "end": v(-16.5, -14.29) * mm});
            skCircle(sketch, "E338.MirrorC", {"center": v(-24.75, -14.29) * mm, "radius": 7.14 * mm, "construction": true});
            skLineSegment(sketch, "E339.MirrorCS", {"start": v(-27.5, -19.05) * mm, "end": v(-30.25, -14.29) * mm});
            skLineSegment(sketch, "E340.MirrorCS", {"start": v(-27.5, -9.53) * mm, "end": v(-22, -9.53) * mm});
            skLineSegment(sketch, "E341.MirrorCS", {"start": v(-30.25, -14.29) * mm, "end": v(-27.5, -9.53) * mm});
            skLineSegment(sketch, "E342.MirrorCS", {"start": v(-33, -14.29) * mm, "end": v(-28.87, -7.14) * mm});
            skCircle(sketch, "E343.MirrorC", {"center": v(-24.75, -14.29) * mm, "radius": 4.76 * mm, "construction": true});
            skLineSegment(sketch, "E344.MirrorCS", {"start": v(-16.5, -14.29) * mm, "end": v(-20.62, -21.43) * mm});
            skPoint(sketch, "E345.MirrorP", {"position": v(-20.62, -11.9) * mm});
            skPoint(sketch, "E346.MirrorP", {"position": v(-18.56, -10.72) * mm});
            skLineSegment(sketch, "E347.MirrorCS", {"start": v(-28.87, -21.43) * mm, "end": v(-33, -14.29) * mm});
            skLineSegment(sketch, "E348.MirrorCS", {"start": v(-22, -19.05) * mm, "end": v(-27.5, -19.05) * mm});
            skLineSegment(sketch, "E349.MirrorCS", {"start": v(-28.87, -7.14) * mm, "end": v(-20.62, -7.14) * mm});
            skLineSegment(sketch, "E350.MirrorCS", {"start": v(-19.25, -14.29) * mm, "end": v(-22, -19.05) * mm});
            skLineSegment(sketch, "E351.MirrorCS", {"start": v(-8.25, -28.58) * mm, "end": v(-16.5, -28.58) * mm});
            skLineSegment(sketch, "E352.MirrorCS", {"start": v(-9.62, -16.67) * mm, "end": v(-6.87, -21.43) * mm});
            skLineSegment(sketch, "E353.MirrorCS", {"start": v(-8.25, -14.29) * mm, "end": v(-4.12, -21.43) * mm});
            skCircle(sketch, "E354.MirrorC", {"center": v(-12.37, -21.43) * mm, "radius": 7.14 * mm, "construction": true});
            skLineSegment(sketch, "E355.MirrorCS", {"start": v(-15.12, -26.2) * mm, "end": v(-17.87, -21.43) * mm});
            skLineSegment(sketch, "E356.MirrorCS", {"start": v(-15.12, -16.67) * mm, "end": v(-9.62, -16.67) * mm});
            skLineSegment(sketch, "E357.MirrorCS", {"start": v(-17.87, -21.43) * mm, "end": v(-15.12, -16.67) * mm});
            skLineSegment(sketch, "E358.MirrorCS", {"start": v(-20.62, -21.43) * mm, "end": v(-16.5, -14.29) * mm});
            skCircle(sketch, "E359.MirrorC", {"center": v(-12.37, -21.43) * mm, "radius": 4.76 * mm, "construction": true});
            skLineSegment(sketch, "E360.MirrorCS", {"start": v(-4.12, -21.43) * mm, "end": v(-8.25, -28.58) * mm});
            skPoint(sketch, "E361.MirrorP", {"position": v(-8.25, -19.05) * mm});
            skPoint(sketch, "E362.MirrorP", {"position": v(-6.19, -17.86) * mm});
            skLineSegment(sketch, "E363.MirrorCS", {"start": v(-16.5, -28.58) * mm, "end": v(-20.62, -21.43) * mm});
            skLineSegment(sketch, "E364.MirrorCS", {"start": v(-9.62, -26.2) * mm, "end": v(-15.12, -26.2) * mm});
            skLineSegment(sketch, "E365.MirrorCS", {"start": v(-16.5, -14.29) * mm, "end": v(-8.25, -14.29) * mm});
            skLineSegment(sketch, "E366.MirrorCS", {"start": v(-6.87, -21.43) * mm, "end": v(-9.62, -26.2) * mm});
            skLineSegment(sketch, "E367.MirrorCS", {"start": v(4.12, -35.72) * mm, "end": v(-4.12, -35.72) * mm});
            skLineSegment(sketch, "E368.MirrorCS", {"start": v(2.75, -23.81) * mm, "end": v(5.5, -28.58) * mm});
            skLineSegment(sketch, "E369.MirrorCS", {"start": v(4.12, -21.43) * mm, "end": v(8.25, -28.58) * mm});
            skCircle(sketch, "E370.MirrorC", {"center": v(0, -28.58) * mm, "radius": 7.14 * mm, "construction": true});
            skLineSegment(sketch, "E371.MirrorCS", {"start": v(-2.75, -33.34) * mm, "end": v(-5.5, -28.58) * mm});
            skLineSegment(sketch, "E372.MirrorCS", {"start": v(-2.75, -23.81) * mm, "end": v(2.75, -23.81) * mm});
            skLineSegment(sketch, "E373.MirrorCS", {"start": v(-5.5, -28.58) * mm, "end": v(-2.75, -23.81) * mm});
            skLineSegment(sketch, "E374.MirrorCS", {"start": v(-8.25, -28.58) * mm, "end": v(-4.12, -21.43) * mm});
            skCircle(sketch, "E375.MirrorC", {"center": v(0, -28.58) * mm, "radius": 4.76 * mm, "construction": true});
            skLineSegment(sketch, "E376.MirrorCS", {"start": v(8.25, -28.58) * mm, "end": v(4.12, -35.72) * mm});
            skPoint(sketch, "E377.MirrorP", {"position": v(4.12, -26.2) * mm});
            skPoint(sketch, "E378.MirrorP", {"position": v(6.19, -25) * mm});
            skLineSegment(sketch, "E379.MirrorCS", {"start": v(-4.12, -35.72) * mm, "end": v(-8.25, -28.58) * mm});
            skLineSegment(sketch, "E380.MirrorCS", {"start": v(2.75, -33.34) * mm, "end": v(-2.75, -33.34) * mm});
            skLineSegment(sketch, "E381.MirrorCS", {"start": v(-4.12, -21.43) * mm, "end": v(4.12, -21.43) * mm});
            skLineSegment(sketch, "E382.MirrorCS", {"start": v(5.5, -28.57) * mm, "end": v(2.75, -33.34) * mm});
            skLineSegment(sketch, "E383.MirrorCS", {"start": v(15.12, -30.96) * mm, "end": v(16.95, -34.12) * mm});
            skLineSegment(sketch, "E384.MirrorCS", {"start": v(16.5, -28.58) * mm, "end": v(19.05, -33) * mm});
            skArc(sketch, "E385.MirrorC", {"start": v(19, -33.03) * mm, "mid": v(10.03, -28.97) * mm, "end": v(5.5, -37.7) * mm, "construction": true});
            skLineSegment(sketch, "E386.MirrorCS", {"start": v(9.62, -30.96) * mm, "end": v(15.12, -30.96) * mm});
            skLineSegment(sketch, "E387.MirrorCS", {"start": v(6.87, -35.72) * mm, "end": v(9.62, -30.96) * mm});
            skLineSegment(sketch, "E388.MirrorCS", {"start": v(4.12, -35.72) * mm, "end": v(8.25, -28.58) * mm});
            skArc(sketch, "E389.MirrorC", {"start": v(16.87, -34.16) * mm, "mid": v(10.81, -31.22) * mm, "end": v(7.87, -37.28) * mm, "construction": true});
            skPoint(sketch, "E390.MirrorP", {"position": v(16.5, -33.34) * mm});
            skPoint(sketch, "E391.MirrorP", {"position": v(18.56, -32.15) * mm});
            skLineSegment(sketch, "E392.MirrorCS", {"start": v(8.25, -28.58) * mm, "end": v(16.5, -28.58) * mm});
            skLineSegment(sketch, "E393.MirrorCS", {"start": v(-33, -14.29) * mm, "end": v(-28.87, -21.43) * mm});
            skArc(sketch, "E394.MirrorC", {"start": v(-30.2, -23.22) * mm, "mid": v(-30.93, -17.86) * mm, "end": v(-35.21, -14.55) * mm, "construction": true});
            skLineSegment(sketch, "E395.MirrorCS", {"start": v(-28.87, -21.43) * mm, "end": v(-30.03, -23.44) * mm});
            skPoint(sketch, "E396.MirrorP", {"position": v(-33, -19.05) * mm});
            skPoint(sketch, "E397.MirrorP", {"position": v(-30.93, -17.86) * mm});
            skLineSegment(sketch, "E398.MirrorCS", {"start": v(-22, -23.81) * mm, "end": v(-19.25, -28.58) * mm});
            skLineSegment(sketch, "E399.MirrorCS", {"start": v(-20.62, -21.43) * mm, "end": v(-16.5, -28.58) * mm});
            skArc(sketch, "E400.MirrorC", {"start": v(-19.1, -32.96) * mm, "mid": v(-20.07, -23.17) * mm, "end": v(-29.9, -23.62) * mm, "construction": true});
            skLineSegment(sketch, "E401.MirrorCS", {"start": v(-27.5, -23.81) * mm, "end": v(-22, -23.81) * mm});
            skArc(sketch, "E402.MirrorC", {"start": v(-21.15, -31.7) * mm, "mid": v(-21.63, -24.97) * mm, "end": v(-28.35, -25.46) * mm, "construction": true});
            skLineSegment(sketch, "E403.MirrorCS", {"start": v(-16.5, -28.58) * mm, "end": v(-19.05, -33) * mm});
            skPoint(sketch, "E404.MirrorP", {"position": v(-20.62, -26.2) * mm});
            skPoint(sketch, "E405.MirrorP", {"position": v(-18.56, -25) * mm});
            skLineSegment(sketch, "E406.MirrorCS", {"start": v(-28.87, -21.43) * mm, "end": v(-20.62, -21.43) * mm});
            skLineSegment(sketch, "E407.MirrorCS", {"start": v(-19.25, -28.58) * mm, "end": v(-21.07, -31.74) * mm});
            skLineSegment(sketch, "E408.MirrorCS", {"start": v(-9.62, -30.96) * mm, "end": v(-6.87, -35.72) * mm});
            skLineSegment(sketch, "E409.MirrorCS", {"start": v(-8.25, -28.58) * mm, "end": v(-4.12, -35.72) * mm});
            skArc(sketch, "E410.MirrorC", {"start": v(-5.5, -37.7) * mm, "mid": v(-10.03, -28.97) * mm, "end": v(-19, -33.03) * mm, "construction": true});
            skLineSegment(sketch, "E411.MirrorCS", {"start": v(-15.12, -30.96) * mm, "end": v(-9.62, -30.96) * mm});
            skLineSegment(sketch, "E412.MirrorCS", {"start": v(-16.95, -34.12) * mm, "end": v(-15.12, -30.96) * mm});
            skLineSegment(sketch, "E413.MirrorCS", {"start": v(-19.05, -33) * mm, "end": v(-16.5, -28.58) * mm});
            skArc(sketch, "E414.MirrorC", {"start": v(-7.87, -37.28) * mm, "mid": v(-10.81, -31.22) * mm, "end": v(-16.87, -34.16) * mm, "construction": true});
            skLineSegment(sketch, "E415.MirrorCS", {"start": v(-4.12, -35.72) * mm, "end": v(-5.29, -37.73) * mm});
            skPoint(sketch, "E416.MirrorP", {"position": v(-8.25, -33.34) * mm});
            skPoint(sketch, "E417.MirrorP", {"position": v(-6.19, -32.15) * mm});
            skLineSegment(sketch, "E418.MirrorCS", {"start": v(-16.5, -28.58) * mm, "end": v(-8.25, -28.58) * mm});
            skLineSegment(sketch, "E419.MirrorCS", {"start": v(-6.87, -35.72) * mm, "end": v(-7.78, -37.3) * mm});
            skLineSegment(sketch, "E420.MirrorCS", {"start": v(4.12, -35.72) * mm, "end": v(5.29, -37.73) * mm});
            skArc(sketch, "E421.MirrorC", {"start": v(5, -37.77) * mm, "mid": v(0, -35.72) * mm, "end": v(-5, -37.77) * mm, "construction": true});
            skLineSegment(sketch, "E422.MirrorCS", {"start": v(-4.12, -35.72) * mm, "end": v(4.12, -35.72) * mm});
            skLineSegment(sketch, "E423.trimOffspring", {"start": v(-7.78, 37.3) * mm, "end": v(-6.87, 35.72) * mm});
            skLineSegment(sketch, "E424.trimOffspring", {"start": v(-5.29, 37.73) * mm, "end": v(-4.12, 35.72) * mm});
            skLineSegment(sketch, "E425.trimOffspring", {"start": v(5.29, 37.73) * mm, "end": v(4.12, 35.72) * mm});
            skLineSegment(sketch, "E426.trimOffspring", {"start": v(28.4, 25.39) * mm, "end": v(27.5, 23.81) * mm});
            skLineSegment(sketch, "E427.trimOffspring", {"start": v(30.03, 23.44) * mm, "end": v(28.87, 21.43) * mm});
            skLineSegment(sketch, "E428.trimOffspring", {"start": v(35.32, 14.29) * mm, "end": v(33, 14.29) * mm});
            skLineSegment(sketch, "E429.trimOffspring", {"start": v(36.2, -11.9) * mm, "end": v(34.37, -11.9) * mm});
            skLineSegment(sketch, "E430.trimOffspring", {"start": v(35.32, -14.29) * mm, "end": v(33, -14.29) * mm});
            skLineSegment(sketch, "E431.trimOffspring", {"start": v(30.03, -23.44) * mm, "end": v(28.87, -21.43) * mm});
            skLineSegment(sketch, "E432.trimOffspring", {"start": v(7.78, -37.3) * mm, "end": v(6.87, -35.72) * mm});
            skLineSegment(sketch, "E433.trimOffspring", {"start": v(5.29, -37.73) * mm, "end": v(4.12, -35.72) * mm});
            skLineSegment(sketch, "E434.trimOffspring", {"start": v(-5.29, -37.73) * mm, "end": v(-4.12, -35.72) * mm});
            skLineSegment(sketch, "E435.trimOffspring", {"start": v(-28.4, -25.39) * mm, "end": v(-27.5, -23.81) * mm});
            skLineSegment(sketch, "E436.trimOffspring", {"start": v(-30.03, -23.44) * mm, "end": v(-28.87, -21.43) * mm});
            skLineSegment(sketch, "E437.trimOffspring", {"start": v(-35.32, -14.29) * mm, "end": v(-33, -14.29) * mm});
            skLineSegment(sketch, "E438.trimOffspring", {"start": v(-36.2, 11.9) * mm, "end": v(-34.37, 11.9) * mm});
            skLineSegment(sketch, "E439.trimOffspring", {"start": v(-35.32, 14.29) * mm, "end": v(-33, 14.29) * mm});
            skArc(sketch, "E440.trimOffspring", {"start": v(-29.9, 23.62) * mm, "mid": v(-20.07, 23.17) * mm, "end": v(-19.1, 32.96) * mm, "construction": true});
            skLineSegment(sketch, "E441.trimOffspring", {"start": v(-30.03, 23.44) * mm, "end": v(-28.87, 21.43) * mm});
            skArc(sketch, "E442.trimOffspring", {"start": v(-28.35, 25.46) * mm, "mid": v(-21.63, 24.97) * mm, "end": v(-21.15, 31.7) * mm, "construction": true});
            skSolve(sketch);
        }
        {
            var Q0;
            Q0=makeQuery(id+"F0.imprint","IMPRINT",FACE,{"disambiguationData":[TD([[makeQuery(id+"F0.imprint","IMPRINT",EDGE,{"derivedFrom":sQuery(id+"F0.wireOp",EDGE,"E1.4")}),1.0]])]});
            var Q1;
            Q1=makeQuery(id+"F0.imprint","IMPRINT",FACE,{"disambiguationData":[TD([[makeQuery(id+"F0.imprint","IMPRINT",EDGE,{"derivedFrom":sQuery(id+"F0.wireOp",EDGE,"E352.MirrorCS")}),1.0]])]});
            var Q2;
            Q2=makeQuery(id+"F0.imprint","IMPRINT",FACE,{"disambiguationData":[TD([[makeQuery(id+"F0.imprint","IMPRINT",EDGE,{"derivedFrom":sQuery(id+"F0.wireOp",EDGE,"E81.MirrorCS")}),-1.0]])]});
            var Q3;
            Q3=makeQuery(id+"F0.imprint","IMPRINT",FACE,{"disambiguationData":[TD([[makeQuery(id+"F0.imprint","IMPRINT",EDGE,{"derivedFrom":sQuery(id+"F0.wireOp",EDGE,"E239.MirrorCS")}),-1.0]])]});
            var Q4;
            {var subQ1=sQuery(id+"F0.wireOp",EDGE,"E168.MirrorCS");Q4=makeQuery(id+"F0.imprint","IMPRINT",FACE,{"disambiguationData":[TD([[makeQuery(id+"F0.imprint","IMPRINT",EDGE,{"derivedFrom":subQ1}),-1.0]])]});}
            var Q5;
            Q5=makeQuery(id+"F0.imprint","IMPRINT",FACE,{"disambiguationData":[TD([[makeQuery(id+"F0.imprint","IMPRINT",EDGE,{"derivedFrom":sQuery(id+"F0.wireOp",EDGE,"E164.MirrorCS")}),-1.0]])]});
            var Q6;
            Q6=makeQuery(id+"F0.imprint","IMPRINT",FACE,{"disambiguationData":[TD([[makeQuery(id+"F0.imprint","IMPRINT",EDGE,{"derivedFrom":sQuery(id+"F0.wireOp",EDGE,"E336.MirrorCS")}),-1.0]])]});
            var Q7;
            Q7=makeQuery(id+"F0.imprint","IMPRINT",FACE,{"disambiguationData":[TD([[makeQuery(id+"F0.imprint","IMPRINT",EDGE,{"derivedFrom":sQuery(id+"F0.wireOp",EDGE,"E291.MirrorCS")}),-1.0]])]});
            var Q8;
            Q8=makeQuery(id+"F0.imprint","IMPRINT",FACE,{"disambiguationData":[TD([[makeQuery(id+"F0.imprint","IMPRINT",EDGE,{"derivedFrom":sQuery(id+"F0.wireOp",EDGE,"E194.MirrorCS")}),1.0]])]});
            var Q9;
            Q9=makeQuery(id+"F0.imprint","IMPRINT",FACE,{"disambiguationData":[TD([[makeQuery(id+"F0.imprint","IMPRINT",EDGE,{"derivedFrom":sQuery(id+"F0.wireOp",EDGE,"E49.MirrorCS")}),-1.0]])]});
            var Q10;
            Q10=makeQuery(id+"F0.imprint","IMPRINT",FACE,{"disambiguationData":[TD([[makeQuery(id+"F0.imprint","IMPRINT",EDGE,{"derivedFrom":sQuery(id+"F0.wireOp",EDGE,"E398.MirrorCS")}),1.0]])]});
            var Q11;
            Q11=makeQuery(id+"F0.imprint","IMPRINT",FACE,{"disambiguationData":[TD([[makeQuery(id+"F0.imprint","IMPRINT",EDGE,{"derivedFrom":sQuery(id+"F0.wireOp",EDGE,"E239.MirrorCS")}),1.0]])]});
            var Q12;
            Q12=makeQuery(id+"F0.imprint","IMPRINT",FACE,{"disambiguationData":[TD([[makeQuery(id+"F0.imprint","IMPRINT",EDGE,{"derivedFrom":sQuery(id+"F0.wireOp",EDGE,"E393.MirrorCS")}),-1.0]])]});
            var Q13;
            Q13=makeQuery(id+"F0.imprint","IMPRINT",FACE,{"disambiguationData":[TD([[makeQuery(id+"F0.imprint","IMPRINT",EDGE,{"derivedFrom":sQuery(id+"F0.wireOp",EDGE,"E320.MirrorCS")}),1.0]])]});
            var Q14;
            Q14=makeQuery(id+"F0.imprint","IMPRINT",FACE,{"disambiguationData":[TD([[makeQuery(id+"F0.imprint","IMPRINT",EDGE,{"derivedFrom":sQuery(id+"F0.wireOp",EDGE,"E213.MirrorCS")}),-1.0]])]});
            var Q15;
            {var subQ0=sQuery(id+"F0.wireOp",EDGE,"E158.MirrorCS");Q15=makeQuery(id+"F0.imprint","IMPRINT",FACE,{"disambiguationData":[TD([[makeQuery(id+"F0.imprint","IMPRINT",EDGE,{"derivedFrom":subQ0}),-1.0]])]});}
            var Q16;
            Q16=makeQuery(id+"F0.imprint","IMPRINT",FACE,{"disambiguationData":[TD([[makeQuery(id+"F0.imprint","IMPRINT",EDGE,{"derivedFrom":sQuery(id+"F0.wireOp",EDGE,"E223.MirrorCS")}),1.0]])]});
            var Q17;
            Q17=makeQuery(id+"F0.imprint","IMPRINT",FACE,{"disambiguationData":[TD([[makeQuery(id+"F0.imprint","IMPRINT",EDGE,{"derivedFrom":sQuery(id+"F0.wireOp",EDGE,"E50.MirrorCS")}),-1.0]])]});
            var Q18;
            Q18=makeQuery(id+"F0.imprint","IMPRINT",FACE,{"disambiguationData":[TD([[makeQuery(id+"F0.imprint","IMPRINT",EDGE,{"derivedFrom":sQuery(id+"F0.wireOp",EDGE,"E213.MirrorCS")}),1.0]])]});
            var Q19;
            Q19=makeQuery(id+"F0.imprint","IMPRINT",FACE,{"disambiguationData":[TD([[makeQuery(id+"F0.imprint","IMPRINT",EDGE,{"derivedFrom":sQuery(id+"F0.wireOp",EDGE,"E267.MirrorCS")}),1.0]])]});
            var Q20;
            Q20=makeQuery(id+"F0.imprint","IMPRINT",FACE,{"disambiguationData":[TD([[makeQuery(id+"F0.imprint","IMPRINT",EDGE,{"derivedFrom":sQuery(id+"F0.wireOp",EDGE,"E178.MirrorCS")}),-1.0]])]});
            var Q21;
            Q21=makeQuery(id+"F0.imprint","IMPRINT",FACE,{"disambiguationData":[TD([[makeQuery(id+"F0.imprint","IMPRINT",EDGE,{"derivedFrom":sQuery(id+"F0.wireOp",EDGE,"E130.MirrorCS")}),1.0]])]});
            var Q22;
            Q22=makeQuery(id+"F0.imprint","IMPRINT",FACE,{"disambiguationData":[TD([[makeQuery(id+"F0.imprint","IMPRINT",EDGE,{"derivedFrom":sQuery(id+"F0.wireOp",EDGE,"E2.MirrorCS")}),1.0]])]});
            var Q23;
            Q23=makeQuery(id+"F0.imprint","IMPRINT",FACE,{"disambiguationData":[TD([[makeQuery(id+"F0.imprint","IMPRINT",EDGE,{"derivedFrom":sQuery(id+"F0.wireOp",EDGE,"E211.MirrorCS")}),-1.0]])]});
            var Q24;
            Q24=makeQuery(id+"F0.imprint","IMPRINT",FACE,{"disambiguationData":[TD([[makeQuery(id+"F0.imprint","IMPRINT",EDGE,{"derivedFrom":sQuery(id+"F0.wireOp",EDGE,"E0.0")}),1.0]])]});
            var Q25;
            Q25=makeQuery(id+"F0.imprint","IMPRINT",FACE,{"disambiguationData":[TD([[makeQuery(id+"F0.imprint","IMPRINT",EDGE,{"derivedFrom":sQuery(id+"F0.wireOp",EDGE,"E336.MirrorCS")}),1.0]])]});
            var Q26;
            Q26=makeQuery(id+"F0.imprint","IMPRINT",FACE,{"disambiguationData":[TD([[makeQuery(id+"F0.imprint","IMPRINT",EDGE,{"derivedFrom":sQuery(id+"F0.wireOp",EDGE,"E65.MirrorCS")}),-1.0]])]});
            var Q27;
            Q27=makeQuery(id+"F0.imprint","IMPRINT",FACE,{"disambiguationData":[TD([[makeQuery(id+"F0.imprint","IMPRINT",EDGE,{"derivedFrom":sQuery(id+"F0.wireOp",EDGE,"E0.0")}),-1.0]])]});
            var Q28;
            Q28=makeQuery(id+"F0.imprint","IMPRINT",FACE,{"disambiguationData":[TD([[makeQuery(id+"F0.imprint","IMPRINT",EDGE,{"derivedFrom":sQuery(id+"F0.wireOp",EDGE,"E120.MirrorCS")}),-1.0]])]});
            var Q29;
            Q29=makeQuery(id+"F0.imprint","IMPRINT",FACE,{"disambiguationData":[TD([[makeQuery(id+"F0.imprint","IMPRINT",EDGE,{"derivedFrom":sQuery(id+"F0.wireOp",EDGE,"E307.MirrorCS")}),-1.0]])]});
            var Q30;
            Q30=makeQuery(id+"F0.imprint","IMPRINT",FACE,{"disambiguationData":[TD([[makeQuery(id+"F0.imprint","IMPRINT",EDGE,{"derivedFrom":sQuery(id+"F0.wireOp",EDGE,"E141.MirrorCS")}),-1.0]])]});
            var Q31;
            Q31=makeQuery(id+"F0.imprint","IMPRINT",FACE,{"disambiguationData":[TD([[makeQuery(id+"F0.imprint","IMPRINT",EDGE,{"derivedFrom":sQuery(id+"F0.wireOp",EDGE,"E9.MirrorCS")}),-1.0]])]});
            var Q32;
            Q32=makeQuery(id+"F0.imprint","IMPRINT",FACE,{"disambiguationData":[TD([[makeQuery(id+"F0.imprint","IMPRINT",EDGE,{"derivedFrom":sQuery(id+"F0.wireOp",EDGE,"E112.MirrorCS")}),-1.0]])]});
            var Q33;
            Q33=makeQuery(id+"F0.imprint","IMPRINT",FACE,{"disambiguationData":[TD([[makeQuery(id+"F0.imprint","IMPRINT",EDGE,{"derivedFrom":sQuery(id+"F0.wireOp",EDGE,"E130.MirrorCS")}),-1.0]])]});
            var Q34;
            Q34=makeQuery(id+"F0.imprint","IMPRINT",FACE,{"disambiguationData":[TD([[makeQuery(id+"F0.imprint","IMPRINT",EDGE,{"derivedFrom":sQuery(id+"F0.wireOp",EDGE,"E3.MirrorCS")}),-1.0]])]});
            var Q35;
            Q35=makeQuery(id+"F0.imprint","IMPRINT",FACE,{"disambiguationData":[TD([[makeQuery(id+"F0.imprint","IMPRINT",EDGE,{"derivedFrom":sQuery(id+"F0.wireOp",EDGE,"E422.MirrorCS")}),-1.0]])]});
            var Q36;
            Q36=makeQuery(id+"F0.imprint","IMPRINT",FACE,{"disambiguationData":[TD([[makeQuery(id+"F0.imprint","IMPRINT",EDGE,{"derivedFrom":sQuery(id+"F0.wireOp",EDGE,"E368.MirrorCS")}),1.0]])]});
            var Q37;
            Q37=makeQuery(id+"F0.imprint","IMPRINT",FACE,{"disambiguationData":[TD([[makeQuery(id+"F0.imprint","IMPRINT",EDGE,{"derivedFrom":sQuery(id+"F0.wireOp",EDGE,"E96.MirrorCS")}),-1.0]])]});
            var Q38;
            Q38=makeQuery(id+"F0.imprint","IMPRINT",FACE,{"disambiguationData":[TD([[makeQuery(id+"F0.imprint","IMPRINT",EDGE,{"derivedFrom":sQuery(id+"F0.wireOp",EDGE,"E17.MirrorCS")}),-1.0]])]});
            var Q39;
            Q39=makeQuery(id+"F0.imprint","IMPRINT",FACE,{"disambiguationData":[TD([[makeQuery(id+"F0.imprint","IMPRINT",EDGE,{"derivedFrom":sQuery(id+"F0.wireOp",EDGE,"E178.MirrorCS")}),1.0]])]});
            var Q40;
            Q40=makeQuery(id+"F0.imprint","IMPRINT",FACE,{"disambiguationData":[TD([[makeQuery(id+"F0.imprint","IMPRINT",EDGE,{"derivedFrom":sQuery(id+"F0.wireOp",EDGE,"E267.MirrorCS")}),-1.0]])]});
            var Q41;
            Q41=makeQuery(id+"F0.imprint","IMPRINT",FACE,{"disambiguationData":[TD([[makeQuery(id+"F0.imprint","IMPRINT",EDGE,{"derivedFrom":sQuery(id+"F0.wireOp",EDGE,"E64.MirrorCS")}),-1.0]])]});
            var Q42;
            Q42=makeQuery(id+"F0.imprint","IMPRINT",FACE,{"disambiguationData":[TD([[makeQuery(id+"F0.imprint","IMPRINT",EDGE,{"derivedFrom":sQuery(id+"F0.wireOp",EDGE,"E194.MirrorCS")}),-1.0]])]});
            var Q43;
            Q43=makeQuery(id+"F0.imprint","IMPRINT",FACE,{"disambiguationData":[TD([[makeQuery(id+"F0.imprint","IMPRINT",EDGE,{"derivedFrom":sQuery(id+"F0.wireOp",EDGE,"E368.MirrorCS")}),-1.0]])]});
            var Q44;
            {var subQ1=sQuery(id+"F0.wireOp",EDGE,"E383.MirrorCS");Q44=makeQuery(id+"F0.imprint","IMPRINT",FACE,{"disambiguationData":[TD([[makeQuery(id+"F0.imprint","IMPRINT",EDGE,{"derivedFrom":subQ1}),1.0]])]});}
            var Q45;
            Q45=makeQuery(id+"F0.imprint","IMPRINT",FACE,{"disambiguationData":[TD([[makeQuery(id+"F0.imprint","IMPRINT",EDGE,{"derivedFrom":sQuery(id+"F0.wireOp",EDGE,"E275.MirrorCS")}),1.0]])]});
            var Q46;
            {var subQ1=sQuery(id+"F0.wireOp",EDGE,"E309.MirrorCS");Q46=makeQuery(id+"F0.imprint","IMPRINT",FACE,{"disambiguationData":[TD([[makeQuery(id+"F0.imprint","IMPRINT",EDGE,{"derivedFrom":subQ1}),-1.0]])]});}
            var Q47;
            Q47=makeQuery(id+"F0.imprint","IMPRINT",FACE,{"disambiguationData":[TD([[makeQuery(id+"F0.imprint","IMPRINT",EDGE,{"derivedFrom":sQuery(id+"F0.wireOp",EDGE,"E141.MirrorCS")}),1.0]])]});
            var Q48;
            Q48=makeQuery(id+"F0.imprint","IMPRINT",FACE,{"disambiguationData":[TD([[makeQuery(id+"F0.imprint","IMPRINT",EDGE,{"derivedFrom":sQuery(id+"F0.wireOp",EDGE,"E408.MirrorCS")}),1.0]])]});
            var Q49;
            Q49=makeQuery(id+"F0.imprint","IMPRINT",FACE,{"disambiguationData":[TD([[makeQuery(id+"F0.imprint","IMPRINT",EDGE,{"derivedFrom":sQuery(id+"F0.wireOp",EDGE,"E352.MirrorCS")}),-1.0]])]});
            var Q50;
            Q50=makeQuery(id+"F0.imprint","IMPRINT",FACE,{"disambiguationData":[TD([[makeQuery(id+"F0.imprint","IMPRINT",EDGE,{"derivedFrom":sQuery(id+"F0.wireOp",EDGE,"E251.MirrorCS")}),1.0]])]});
            var Q51;
            Q51=makeQuery(id+"F0.imprint","IMPRINT",FACE,{"disambiguationData":[TD([[makeQuery(id+"F0.imprint","IMPRINT",EDGE,{"derivedFrom":sQuery(id+"F0.wireOp",EDGE,"E34.MirrorCS")}),-1.0]])]});
            var Q52;
            {var subQ0=sQuery(id+"F0.wireOp",EDGE,"E168.MirrorCS");Q52=makeQuery(id+"F0.imprint","IMPRINT",FACE,{"disambiguationData":[TD([[makeQuery(id+"F0.imprint","IMPRINT",EDGE,{"derivedFrom":subQ0}),1.0]])]});}
            var Q53;
            Q53=makeQuery(id+"F0.imprint","IMPRINT",FACE,{"disambiguationData":[TD([[makeQuery(id+"F0.imprint","IMPRINT",EDGE,{"derivedFrom":sQuery(id+"F0.wireOp",EDGE,"E251.MirrorCS")}),-1.0]])]});
            var Q54;
            {var subQ1=sQuery(id+"F0.wireOp",EDGE,"E309.MirrorCS");Q54=makeQuery(id+"F0.imprint","IMPRINT",FACE,{"disambiguationData":[TD([[makeQuery(id+"F0.imprint","IMPRINT",EDGE,{"derivedFrom":subQ1}),1.0]])]});}
            var Q55;
            Q55=makeQuery(id+"F0.imprint","IMPRINT",FACE,{"disambiguationData":[TD([[makeQuery(id+"F0.imprint","IMPRINT",EDGE,{"derivedFrom":sQuery(id+"F0.wireOp",EDGE,"E291.MirrorCS")}),1.0]])]});
            var Q56;
            Q56=makeQuery(id+"F0.imprint","IMPRINT",FACE,{"disambiguationData":[TD([[makeQuery(id+"F0.imprint","IMPRINT",EDGE,{"derivedFrom":sQuery(id+"F0.wireOp",EDGE,"E139.MirrorCS")}),-1.0]])]});
            var Q57;
            Q57=makeQuery(id+"F0.imprint","IMPRINT",FACE,{"disambiguationData":[TD([[makeQuery(id+"F0.imprint","IMPRINT",EDGE,{"derivedFrom":sQuery(id+"F0.wireOp",EDGE,"E275.MirrorCS")}),-1.0]])]});
            var Q58;
            Q58=makeQuery(id+"F0.imprint","IMPRINT",FACE,{"disambiguationData":[TD([[makeQuery(id+"F0.imprint","IMPRINT",EDGE,{"derivedFrom":sQuery(id+"F0.wireOp",EDGE,"E95.MirrorCS")}),-1.0]])]});
            var Q59;
            Q59=makeQuery(id+"F0.imprint","IMPRINT",FACE,{"disambiguationData":[TD([[makeQuery(id+"F0.imprint","IMPRINT",EDGE,{"derivedFrom":sQuery(id+"F0.wireOp",EDGE,"E110.MirrorCS")}),-1.0]])]});
            var Q60;
            Q60=makeQuery(id+"F0.imprint","IMPRINT",FACE,{"disambiguationData":[TD([[makeQuery(id+"F0.imprint","IMPRINT",EDGE,{"derivedFrom":sQuery(id+"F0.wireOp",EDGE,"E223.MirrorCS")}),-1.0]])]});
            var Q61;
            Q61=makeQuery(id+"F0.imprint","IMPRINT",FACE,{"disambiguationData":[TD([[makeQuery(id+"F0.imprint","IMPRINT",EDGE,{"derivedFrom":sQuery(id+"F0.wireOp",EDGE,"E118.MirrorCS")}),-1.0]])]});
            var Q62;
            {var subQ0=sQuery(id+"F0.wireOp",EDGE,"E383.MirrorCS");Q62=makeQuery(id+"F0.imprint","IMPRINT",FACE,{"disambiguationData":[TD([[makeQuery(id+"F0.imprint","IMPRINT",EDGE,{"derivedFrom":subQ0}),-1.0]])]});}
            var Q63;
            Q63=makeQuery(id+"F0.imprint","IMPRINT",FACE,{"disambiguationData":[TD([[makeQuery(id+"F0.imprint","IMPRINT",EDGE,{"derivedFrom":sQuery(id+"F0.wireOp",EDGE,"E81.MirrorCS")}),1.0]])]});
            var Q64;
            Q64=makeQuery(id+"F0.imprint","IMPRINT",FACE,{"disambiguationData":[TD([[makeQuery(id+"F0.imprint","IMPRINT",EDGE,{"derivedFrom":sQuery(id+"F0.wireOp",EDGE,"E408.MirrorCS")}),-1.0]])]});
            var Q65;
            Q65=makeQuery(id+"F0.imprint","IMPRINT",FACE,{"disambiguationData":[TD([[makeQuery(id+"F0.imprint","IMPRINT",EDGE,{"derivedFrom":sQuery(id+"F0.wireOp",EDGE,"E320.MirrorCS")}),-1.0]])]});
            var Q66;
            Q66=makeQuery(id+"F0.imprint","IMPRINT",FACE,{"disambiguationData":[TD([[makeQuery(id+"F0.imprint","IMPRINT",EDGE,{"derivedFrom":sQuery(id+"F0.wireOp",EDGE,"E398.MirrorCS")}),-1.0]])]});
            var Q67;
            Q67=makeQuery(id+"F0.imprint","IMPRINT",FACE,{"disambiguationData":[TD([[makeQuery(id+"F0.imprint","IMPRINT",EDGE,{"derivedFrom":sQuery(id+"F0.wireOp",EDGE,"E156.MirrorCS")}),-1.0]])]});
            extrude(context, id + "F1", {"entities" : qUnion([Q0, Q1, Q2, Q3, Q4, Q5, Q6, Q7, Q8, Q9, Q10, Q11, Q12, Q13, Q14, Q15, Q16, Q17, Q18, Q19, Q20, Q21, Q22, Q23, Q24, Q25, Q26, Q27, Q28, Q29, Q30, Q31, Q32, Q33, Q34, Q35, Q36, Q37, Q38, Q39, Q40, Q41, Q42, Q43, Q44, Q45, Q46, Q47, Q48, Q49, Q50, Q51, Q52, Q53, Q54, Q55, Q56, Q57, Q58, Q59, Q60, Q61, Q62, Q63, Q64, Q65, Q66, Q67]), "oppositeDirection" : true, "depth" : 12.7 * mm});
        }
        {
            var Q0;
            Q0=makeQuery(id+"F0.imprint","IMPRINT",FACE,{"disambiguationData":[TD([[makeQuery(id+"F0.imprint","IMPRINT",EDGE,{"derivedFrom":sQuery(id+"F0.wireOp",EDGE,"E141.MirrorCS")}),-1.0]])]});
            var Q1;
            {var subQ0=sQuery(id+"F0.wireOp",EDGE,"E158.MirrorCS");Q1=makeQuery(id+"F0.imprint","IMPRINT",FACE,{"disambiguationData":[TD([[makeQuery(id+"F0.imprint","IMPRINT",EDGE,{"derivedFrom":subQ0}),-1.0]])]});}
            var Q2;
            Q2=makeQuery(id+"F0.imprint","IMPRINT",FACE,{"disambiguationData":[TD([[makeQuery(id+"F0.imprint","IMPRINT",EDGE,{"derivedFrom":sQuery(id+"F0.wireOp",EDGE,"E65.MirrorCS")}),-1.0]])]});
            var Q3;
            Q3=makeQuery(id+"F0.imprint","IMPRINT",FACE,{"disambiguationData":[TD([[makeQuery(id+"F0.imprint","IMPRINT",EDGE,{"derivedFrom":sQuery(id+"F0.wireOp",EDGE,"E120.MirrorCS")}),-1.0]])]});
            var Q4;
            Q4=makeQuery(id+"F0.imprint","IMPRINT",FACE,{"disambiguationData":[TD([[makeQuery(id+"F0.imprint","IMPRINT",EDGE,{"derivedFrom":sQuery(id+"F0.wireOp",EDGE,"E34.MirrorCS")}),-1.0]])]});
            var Q5;
            Q5=makeQuery(id+"F0.imprint","IMPRINT",FACE,{"disambiguationData":[TD([[makeQuery(id+"F0.imprint","IMPRINT",EDGE,{"derivedFrom":sQuery(id+"F0.wireOp",EDGE,"E112.MirrorCS")}),-1.0]])]});
            var Q6;
            Q6=makeQuery(id+"F0.imprint","IMPRINT",FACE,{"disambiguationData":[TD([[makeQuery(id+"F0.imprint","IMPRINT",EDGE,{"derivedFrom":sQuery(id+"F0.wireOp",EDGE,"E96.MirrorCS")}),-1.0]])]});
            var Q7;
            Q7=makeQuery(id+"F0.imprint","IMPRINT",FACE,{"disambiguationData":[TD([[makeQuery(id+"F0.imprint","IMPRINT",EDGE,{"derivedFrom":sQuery(id+"F0.wireOp",EDGE,"E2.MirrorCS")}),1.0]])]});
            var Q8;
            Q8=makeQuery(id+"F0.imprint","IMPRINT",FACE,{"disambiguationData":[TD([[makeQuery(id+"F0.imprint","IMPRINT",EDGE,{"derivedFrom":sQuery(id+"F0.wireOp",EDGE,"E81.MirrorCS")}),-1.0]])]});
            var Q9;
            Q9=makeQuery(id+"F0.imprint","IMPRINT",FACE,{"disambiguationData":[TD([[makeQuery(id+"F0.imprint","IMPRINT",EDGE,{"derivedFrom":sQuery(id+"F0.wireOp",EDGE,"E130.MirrorCS")}),-1.0]])]});
            var Q10;
            Q10=makeQuery(id+"F0.imprint","IMPRINT",FACE,{"disambiguationData":[TD([[makeQuery(id+"F0.imprint","IMPRINT",EDGE,{"derivedFrom":sQuery(id+"F0.wireOp",EDGE,"E50.MirrorCS")}),-1.0]])]});
            var Q11;
            {var subQ1=sQuery(id+"F0.wireOp",EDGE,"E168.MirrorCS");Q11=makeQuery(id+"F0.imprint","IMPRINT",FACE,{"disambiguationData":[TD([[makeQuery(id+"F0.imprint","IMPRINT",EDGE,{"derivedFrom":subQ1}),-1.0]])]});}
            var Q12;
            Q12=makeQuery(id+"F0.imprint","IMPRINT",FACE,{"disambiguationData":[TD([[makeQuery(id+"F0.imprint","IMPRINT",EDGE,{"derivedFrom":sQuery(id+"F0.wireOp",EDGE,"E178.MirrorCS")}),-1.0]])]});
            var Q13;
            Q13=makeQuery(id+"F0.imprint","IMPRINT",FACE,{"disambiguationData":[TD([[makeQuery(id+"F0.imprint","IMPRINT",EDGE,{"derivedFrom":sQuery(id+"F0.wireOp",EDGE,"E194.MirrorCS")}),-1.0]])]});
            var Q14;
            Q14=makeQuery(id+"F0.imprint","IMPRINT",FACE,{"disambiguationData":[TD([[makeQuery(id+"F0.imprint","IMPRINT",EDGE,{"derivedFrom":sQuery(id+"F0.wireOp",EDGE,"E223.MirrorCS")}),-1.0]])]});
            var Q15;
            Q15=makeQuery(id+"F0.imprint","IMPRINT",FACE,{"disambiguationData":[TD([[makeQuery(id+"F0.imprint","IMPRINT",EDGE,{"derivedFrom":sQuery(id+"F0.wireOp",EDGE,"E213.MirrorCS")}),-1.0]])]});
            var Q16;
            Q16=makeQuery(id+"F0.imprint","IMPRINT",FACE,{"disambiguationData":[TD([[makeQuery(id+"F0.imprint","IMPRINT",EDGE,{"derivedFrom":sQuery(id+"F0.wireOp",EDGE,"E0.0")}),-1.0]])]});
            var Q17;
            Q17=makeQuery(id+"F0.imprint","IMPRINT",FACE,{"disambiguationData":[TD([[makeQuery(id+"F0.imprint","IMPRINT",EDGE,{"derivedFrom":sQuery(id+"F0.wireOp",EDGE,"E17.MirrorCS")}),-1.0]])]});
            var Q18;
            Q18=makeQuery(id+"F0.imprint","IMPRINT",FACE,{"disambiguationData":[TD([[makeQuery(id+"F0.imprint","IMPRINT",EDGE,{"derivedFrom":sQuery(id+"F0.wireOp",EDGE,"E275.MirrorCS")}),-1.0]])]});
            var Q19;
            Q19=makeQuery(id+"F0.imprint","IMPRINT",FACE,{"disambiguationData":[TD([[makeQuery(id+"F0.imprint","IMPRINT",EDGE,{"derivedFrom":sQuery(id+"F0.wireOp",EDGE,"E267.MirrorCS")}),-1.0]])]});
            var Q20;
            Q20=makeQuery(id+"F0.imprint","IMPRINT",FACE,{"disambiguationData":[TD([[makeQuery(id+"F0.imprint","IMPRINT",EDGE,{"derivedFrom":sQuery(id+"F0.wireOp",EDGE,"E320.MirrorCS")}),-1.0]])]});
            var Q21;
            Q21=makeQuery(id+"F0.imprint","IMPRINT",FACE,{"disambiguationData":[TD([[makeQuery(id+"F0.imprint","IMPRINT",EDGE,{"derivedFrom":sQuery(id+"F0.wireOp",EDGE,"E291.MirrorCS")}),-1.0]])]});
            var Q22;
            Q22=makeQuery(id+"F0.imprint","IMPRINT",FACE,{"disambiguationData":[TD([[makeQuery(id+"F0.imprint","IMPRINT",EDGE,{"derivedFrom":sQuery(id+"F0.wireOp",EDGE,"E251.MirrorCS")}),-1.0]])]});
            var Q23;
            Q23=makeQuery(id+"F0.imprint","IMPRINT",FACE,{"disambiguationData":[TD([[makeQuery(id+"F0.imprint","IMPRINT",EDGE,{"derivedFrom":sQuery(id+"F0.wireOp",EDGE,"E239.MirrorCS")}),-1.0]])]});
            var Q24;
            Q24=makeQuery(id+"F0.imprint","IMPRINT",FACE,{"disambiguationData":[TD([[makeQuery(id+"F0.imprint","IMPRINT",EDGE,{"derivedFrom":sQuery(id+"F0.wireOp",EDGE,"E336.MirrorCS")}),-1.0]])]});
            var Q25;
            Q25=makeQuery(id+"F0.imprint","IMPRINT",FACE,{"disambiguationData":[TD([[makeQuery(id+"F0.imprint","IMPRINT",EDGE,{"derivedFrom":sQuery(id+"F0.wireOp",EDGE,"E352.MirrorCS")}),-1.0]])]});
            var Q26;
            Q26=makeQuery(id+"F0.imprint","IMPRINT",FACE,{"disambiguationData":[TD([[makeQuery(id+"F0.imprint","IMPRINT",EDGE,{"derivedFrom":sQuery(id+"F0.wireOp",EDGE,"E398.MirrorCS")}),-1.0]])]});
            var Q27;
            Q27=makeQuery(id+"F0.imprint","IMPRINT",FACE,{"disambiguationData":[TD([[makeQuery(id+"F0.imprint","IMPRINT",EDGE,{"derivedFrom":sQuery(id+"F0.wireOp",EDGE,"E408.MirrorCS")}),-1.0]])]});
            var Q28;
            Q28=makeQuery(id+"F0.imprint","IMPRINT",FACE,{"disambiguationData":[TD([[makeQuery(id+"F0.imprint","IMPRINT",EDGE,{"derivedFrom":sQuery(id+"F0.wireOp",EDGE,"E368.MirrorCS")}),-1.0]])]});
            var Q29;
            {var subQ0=sQuery(id+"F0.wireOp",EDGE,"E383.MirrorCS");Q29=makeQuery(id+"F0.imprint","IMPRINT",FACE,{"disambiguationData":[TD([[makeQuery(id+"F0.imprint","IMPRINT",EDGE,{"derivedFrom":subQ0}),-1.0]])]});}
            var Q30;
            {var subQ1=sQuery(id+"F0.wireOp",EDGE,"E309.MirrorCS");Q30=makeQuery(id+"F0.imprint","IMPRINT",FACE,{"disambiguationData":[TD([[makeQuery(id+"F0.imprint","IMPRINT",EDGE,{"derivedFrom":subQ1}),-1.0]])]});}
            extrude(context, id + "F2", {"entities" : qUnion([Q0, Q1, Q2, Q3, Q4, Q5, Q6, Q7, Q8, Q9, Q10, Q11, Q12, Q13, Q14, Q15, Q16, Q17, Q18, Q19, Q20, Q21, Q22, Q23, Q24, Q25, Q26, Q27, Q28, Q29, Q30]), "operationType" : NewBodyOperationType.REMOVE, "endBound" : BoundingType.THROUGH_ALL, "oppositeDirection" : true, "depth" : 12.7 * mm});
        }
    });
